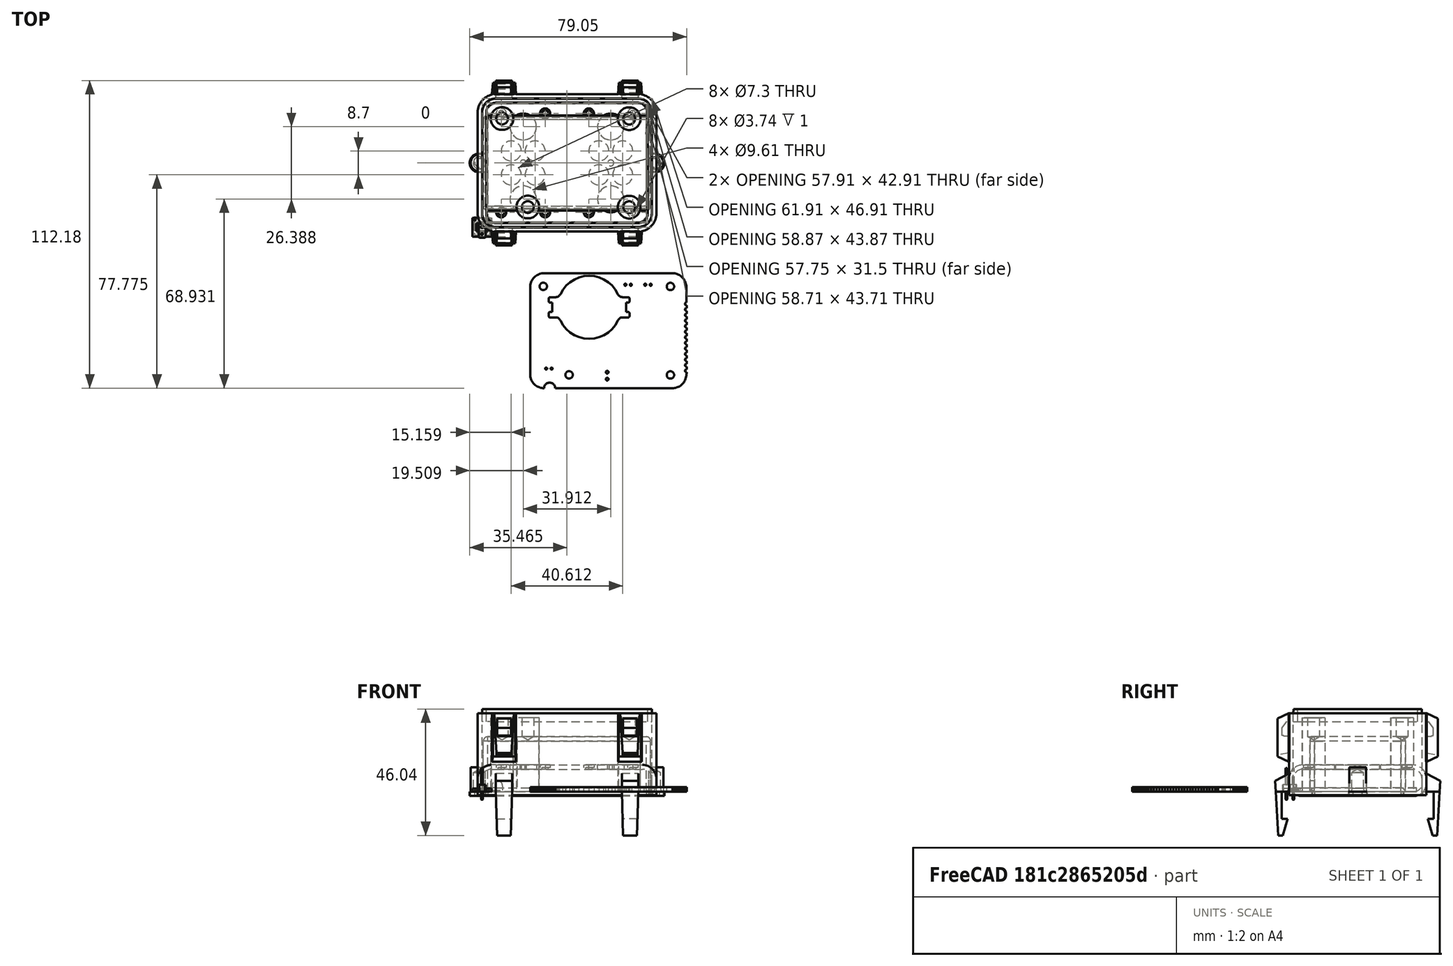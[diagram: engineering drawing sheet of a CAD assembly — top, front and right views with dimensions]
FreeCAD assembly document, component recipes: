
FREECAD ASSEMBLY — COMPONENT RECIPES ("Enclosure")

This assembly document has 16 components, labeled P0..P15 below (a component is one placed body or linked part). 15 of them carry a construction recipe — the FreeCAD feature program that regenerates the part from scratch, quoted from this document or its linked companion documents; the rest are supplied as boundary geometry only. No exploded tour is included for this assembly.
COMPONENT P0 — recipe-attached ("Body002", modeled in this document).
Construction recipe (the document's own serialized feature program — sketch geometry with constraints, then the solid features built on it; lengths are millimeters unless a unit is written):

FEATURE [Sketcher::SketchObject] Sketch003
  FullyConstrained = true
  MapMode = 5
  Support = -> [XY_Plane039]
  expr: Constraints[10] = <<dim>>.encw
  expr: Constraints[9] = <<dim>>.encl
  sketch-geometry (4):
    g0: LineSegment StartX=0 StartY=0 StartZ=0 EndX=61.91 EndY=0 EndZ=0
    g1: LineSegment StartX=61.91 StartY=0 StartZ=0 EndX=61.91 EndY=46.91 EndZ=0
    g2: LineSegment StartX=61.91 StartY=46.91 StartZ=0 EndX=0 EndY=46.91 EndZ=0
    g3: LineSegment StartX=0 StartY=46.91 StartZ=0 EndX=0 EndY=0 EndZ=0
  constraints (11):
    c: Coincident(g0,g1)
    c: Coincident(g1,g2)
    c: Coincident(g2,g3)
    c: Coincident(g3,g0)
    c: Horizontal(g0)
    c: Horizontal(g2)
    c: Vertical(g1)
    c: Vertical(g3)
    c: Coincident(g0,g-1)
    c: Distance(g2) = 61.91
    c: Distance(g1) = 46.91
FEATURE [PartDesign::Pad] Pad002
  Direction = (0,0,1)
  Length = 28.535
  Length2 = 10
  Profile = -> Sketch003
  ReferenceAxis = -> Sketch003 [N_Axis]
  Type = 0
  expr: Length = <<dim>>.ench
FEATURE [PartDesign::Fillet] Fillet001
  Base = -> Pad002 [Edge1,Edge2,Edge3,Edge5,Edge6,Edge8,Edge9,Edge11]
  BaseFeature = -> Pad002
  Radius = 5
  SupportTransform = false
  UseAllEdges = false
  expr: Radius = <<dim>>.encrin
FEATURE [PartDesign::Thickness] Thickness002
  Base = -> Fillet001 [Face2]
  BaseFeature = -> Fillet001
  Intersection = false
  Join = 0
  Mode = 0
  Reversed = true
  SupportTransform = false
  Value = 1.6
  expr: Value = <<dim>>.enctsh
FEATURE [PartDesign::ShapeBinder] ShapeBinder001
  Support = -> [Thickness002]
  TraceSupport = false
FEATURE [PartDesign::SubShapeBinder] Binder
  BindCopyOnChange = 0
  BindMode = 0
  ClaimChildren = false
  Context = -> Part [Body002.Binder.]
  Fuse = false
  MakeFace = true
  OffsetFill = false
  OffsetIntersection = false
  OffsetJoinType = 0
  OffsetOpenResult = false
  PartialLoad = false
  Placement = pos=(0,0,-3) rot=(0,0,1;0rad)
  Relative = true
  Support = -> [ShapeBinder001]
  _Version = 2
  expr: .Placement.Base.z = -<<dim>>.eid
FEATURE [PartDesign::Pocket] Pocket001
  BaseFeature = -> Thickness002
  Direction = (0,0,-1)
  Length = 5
  Length2 = 5
  Profile = -> Binder
  Type = 1
FEATURE [PartDesign::Pad] Pad013
  BaseFeature = -> Pocket001
  Direction = (0,0,1)
  Length = 1.5
  Length2 = 10
  Profile = -> Pocket001 [Face5]
  TaperAngle = -3
  Type = 0
  expr: Length = <<dim>>.elh
  expr: TaperAngle = <<dim>>.elt
FEATURE [PartDesign::Body] Body002
  Group = -> [Sketch003,Pad002,Fillet001,Thickness002,ShapeBinder001,Binder,Pocket001,Pad013]
  Origin = -> Origin041
  Tip = -> Pad013
COMPONENT P1 — recipe-attached ("batteryboxinner", modeled in this document).
Construction recipe (the document's own serialized feature program — sketch geometry with constraints, then the solid features built on it; lengths are millimeters unless a unit is written):

FEATURE [Sketcher::SketchObject] Sketch010
  FullyConstrained = true
  MapMode = 5
  Support = -> [XY_Plane047]
  expr: Constraints[15] = <<dim>>.batl * (1 + <<dim>>.batc)
  expr: Constraints[16] = <<dim>>.batw * (1 + <<dim>>.batc)
  expr: Constraints[26] = <<dim>>.encl / 2
  expr: Constraints[27] = <<dim>>.encw / 2
  sketch-geometry (12):
    g0: LineSegment StartX=2.08 StartY=7.705 StartZ=0 EndX=59.83 EndY=7.705 EndZ=0
    g1: LineSegment StartX=59.83 StartY=7.705 StartZ=0 EndX=59.83 EndY=39.205 EndZ=0
    g2: LineSegment StartX=59.83 StartY=39.205 StartZ=0 EndX=2.08 EndY=39.205 EndZ=0
    g3: LineSegment StartX=2.08 StartY=39.205 StartZ=0 EndX=2.08 EndY=7.705 EndZ=0
    g4: LineSegment StartX=30.955 StartY=23.455 StartZ=0 EndX=2.08 EndY=23.455 EndZ=0
    g5: LineSegment StartX=2.08 StartY=23.455 StartZ=0 EndX=2.08 EndY=7.705 EndZ=0
    g6: LineSegment StartX=2.08 StartY=7.705 StartZ=0 EndX=30.955 EndY=7.705 EndZ=0
    g7: LineSegment StartX=30.955 StartY=7.705 StartZ=0 EndX=30.955 EndY=23.455 EndZ=0
    g8: LineSegment StartX=0 StartY=0 StartZ=0 EndX=30.955 EndY=0 EndZ=0
    g9: LineSegment StartX=30.955 StartY=0 StartZ=0 EndX=30.955 EndY=23.455 EndZ=0
    g10: LineSegment StartX=30.955 StartY=23.455 StartZ=0 EndX=0 EndY=23.455 EndZ=0
    g11: LineSegment StartX=0 StartY=23.455 StartZ=0 EndX=0 EndY=0 EndZ=0
  constraints (31):
    c: Coincident(g0,g1)
    c: Coincident(g1,g2)
    c: Coincident(g2,g3)
    c: Coincident(g3,g0)
    c: Horizontal(g0)
    c: Horizontal(g2)
    c: Vertical(g1)
    c: Vertical(g3)
    c: Coincident(g4,g5)
    c: Coincident(g5,g6)
    c: Coincident(g6,g7)
    c: Coincident(g7,g4)
    c: Horizontal(g4)
    c: Vertical(g7)
    c: Coincident(g5,g0)
    c: Distance(g2) = 57.75
    c: Distance(g1) = 31.5
    c: Coincident(g8,g9)
    c: Coincident(g9,g10)
    c: Coincident(g10,g11)
    c: Coincident(g11,g8)
    c: Horizontal(g8)
    c: Horizontal(g10)
    c: Vertical(g9)
    c: Vertical(g11)
    c: Coincident(g8,g-1)
    c: Distance(g10) = 30.955
    c: Distance(g9) = 23.455
    c: Coincident(g4,g9)
    c: Symmetric(g0,g0,g6)
    c: Symmetric(g0,g2,g4)
FEATURE [PartDesign::Pad] Pad010
  Direction = (0,0,1)
  Length = 18.375
  Length2 = 10
  Profile = -> Sketch010
  ReferenceAxis = -> Sketch010 [N_Axis]
  Type = 0
  expr: Length = <<dim>>.bath * (1 + <<dim>>.batc)
FEATURE [PartDesign::Pad] Pad012
  BaseFeature = -> Pad010
  Direction = (0,0,-1)
  Length = 1.6
  Length2 = 10
  Profile = -> Pad010 [Face5]
  Type = 0
  expr: Length = <<dim>>.enctsh
FEATURE [PartDesign::Body] Body003  label="batteryboxinner"
  Group = -> [Sketch010,Pad010,Pad012]
  Origin = -> Origin048
  Tip = -> Pad012
COMPONENT P2 — recipe-attached ("batteryboxshell", modeled in this document).
Construction recipe (the document's own serialized feature program — sketch geometry with constraints, then the solid features built on it; lengths are millimeters unless a unit is written):

FEATURE [Sketcher::SketchObject] Sketch011
  FullyConstrained = true
  MapMode = 5
  Support = -> [XY_Plane047]
  expr: Constraints[15] = <<dim>>.batl * (1 + <<dim>>.batc)
  expr: Constraints[16] = <<dim>>.batw * (1 + <<dim>>.batc)
  expr: Constraints[26] = <<dim>>.encl / 2
  expr: Constraints[27] = <<dim>>.encw / 2
  sketch-geometry (12):
    g0: LineSegment StartX=2.08 StartY=7.705 StartZ=0 EndX=59.83 EndY=7.705 EndZ=0
    g1: LineSegment StartX=59.83 StartY=7.705 StartZ=0 EndX=59.83 EndY=39.205 EndZ=0
    g2: LineSegment StartX=59.83 StartY=39.205 StartZ=0 EndX=2.08 EndY=39.205 EndZ=0
    g3: LineSegment StartX=2.08 StartY=39.205 StartZ=0 EndX=2.08 EndY=7.705 EndZ=0
    g4: LineSegment StartX=30.955 StartY=23.455 StartZ=0 EndX=2.08 EndY=23.455 EndZ=0
    g5: LineSegment StartX=2.08 StartY=23.455 StartZ=0 EndX=2.08 EndY=7.705 EndZ=0
    g6: LineSegment StartX=2.08 StartY=7.705 StartZ=0 EndX=30.955 EndY=7.705 EndZ=0
    g7: LineSegment StartX=30.955 StartY=7.705 StartZ=0 EndX=30.955 EndY=23.455 EndZ=0
    g8: LineSegment StartX=0 StartY=0 StartZ=0 EndX=30.955 EndY=0 EndZ=0
    g9: LineSegment StartX=30.955 StartY=0 StartZ=0 EndX=30.955 EndY=23.455 EndZ=0
    g10: LineSegment StartX=30.955 StartY=23.455 StartZ=0 EndX=0 EndY=23.455 EndZ=0
    g11: LineSegment StartX=0 StartY=23.455 StartZ=0 EndX=0 EndY=0 EndZ=0
  constraints (31):
    c: Coincident(g0,g1)
    c: Coincident(g1,g2)
    c: Coincident(g2,g3)
    c: Coincident(g3,g0)
    c: Horizontal(g0)
    c: Horizontal(g2)
    c: Vertical(g1)
    c: Vertical(g3)
    c: Coincident(g4,g5)
    c: Coincident(g5,g6)
    c: Coincident(g6,g7)
    c: Coincident(g7,g4)
    c: Horizontal(g4)
    c: Vertical(g7)
    c: Coincident(g5,g0)
    c: Distance(g2) = 57.75
    c: Distance(g1) = 31.5
    c: Coincident(g8,g9)
    c: Coincident(g9,g10)
    c: Coincident(g10,g11)
    c: Coincident(g11,g8)
    c: Horizontal(g8)
    c: Horizontal(g10)
    c: Vertical(g9)
    c: Vertical(g11)
    c: Coincident(g8,g-1)
    c: Distance(g10) = 30.955
    c: Distance(g9) = 23.455
    c: Coincident(g4,g9)
    c: Symmetric(g0,g0,g6)
    c: Symmetric(g0,g2,g4)
FEATURE [PartDesign::Pad] Pad011
  Direction = (0,0,1)
  Length = 18.375
  Length2 = 10
  Profile = -> Sketch011
  ReferenceAxis = -> Sketch011 [N_Axis]
  Type = 0
  expr: Length = <<dim>>.bath * (1 + <<dim>>.batc)
FEATURE [PartDesign::Thickness] Thickness001
  Base = -> Pad011 [Face5]
  BaseFeature = -> Pad011
  Intersection = false
  Join = 0
  Mode = 0
  SupportTransform = false
  Value = 1.6
  expr: Value = <<dim>>.enctsh
FEATURE [Sketcher::SketchObject] Sketch012
  FullyConstrained = false
  MapMode = 5
  Placement = pos=(0,6.105,0) rot=(1,0,0;1.5708rad)
  Support = -> [Thickness001]
  expr: Constraints[10] = <<dim>>.enctsh
  expr: Constraints[11] = <<dim>>.batl * (<<dim>>.batc + 1) / 30
  expr: Constraints[9] = (<<dim>>.encl - <<dim>>.batl * (1 + <<dim>>.batc)) / 2
  sketch-geometry (5):
    g0: ArcOfCircle CenterX=5.55399 CenterY=2.00077 CenterZ=0 NormalX=0 NormalY=0 NormalZ=1 AngleXU=0 Radius=1.925 StartAngle=0 EndAngle=3.14159
    g1: LineSegment StartX=7.47899 StartY=0.400772 StartZ=0 EndX=7.47899 EndY=2.00077 EndZ=0
    g2: LineSegment StartX=3.62899 StartY=2.00077 StartZ=0 EndX=3.62899 EndY=0.400772 EndZ=0
    g3: LineSegment StartX=3.62899 StartY=0.400772 StartZ=0 EndX=7.47899 EndY=0.400772 EndZ=0
    g4: LineSegment StartX=0 StartY=0 StartZ=0 EndX=2.08 EndY=0 EndZ=0
  constraints (12):
    c: Tangent(g1,g0) = -1.5708
    c: Tangent(g0,g2) = -1.5708
    c: Vertical(g1)
    c: Horizontal(g3)
    c: Coincident(g2,g3)
    c: Coincident(g1,g3)
    c: Vertical(g2)
    c: Coincident(g4,g-1)
    c: PointOnObject(g4,g-1)
    c: Distance(g4) = 2.08
    c: Distance(g1,g0) = 1.6
    c: Radius(g0) = 1.925
FEATURE [PartDesign::Pocket] Pocket
  BaseFeature = -> Thickness001
  Direction = (0,1,-2e-16)
  Length = 1.6
  Length2 = 5
  Profile = -> Sketch012
  ReferenceAxis = -> Sketch012 [N_Axis]
  Type = 0
  expr: Length = <<dim>>.enctsh
FEATURE [PartDesign::Body] Body004  label="batteryboxshell"
  Group = -> [Sketch011,Pad011,Thickness001,Sketch012,Pocket]
  Origin = -> Origin049
  Tip = -> Pocket
COMPONENT P3 — recipe-attached ("batterydoorneg", modeled in this document).
Construction recipe (the document's own serialized feature program — sketch geometry with constraints, then the solid features built on it; lengths are millimeters unless a unit is written):

FEATURE [Sketcher::SketchObject] Sketch013
  FullyConstrained = true
  MapMode = 5
  Support = -> [XY_Plane047]
  expr: Constraints[15] = <<dim>>.batl * (1 + <<dim>>.batc) + <<dim>>.enctsh + 2 * <<dim>>.enctol
  expr: Constraints[16] = <<dim>>.batw * (1 + <<dim>>.batc) + <<dim>>.enctsh + 2 * <<dim>>.enctol
  expr: Constraints[26] = <<dim>>.encl / 2
  expr: Constraints[27] = <<dim>>.encw / 2
  expr: Constraints[47] = (<<dim>>.hid + <<dim>>.hit) / 2 + <<dim>>.enctol
  expr: Constraints[48] = <<dim>>.hid / 2
  sketch-geometry (22):
    g0: LineSegment StartX=1.026 StartY=6.651 StartZ=0 EndX=60.884 EndY=6.651 EndZ=0
    g1: LineSegment StartX=60.884 StartY=6.651 StartZ=0 EndX=60.884 EndY=40.259 EndZ=0
    g2: LineSegment StartX=60.884 StartY=40.259 StartZ=0 EndX=1.026 EndY=40.259 EndZ=0
    g3: LineSegment StartX=1.026 StartY=40.259 StartZ=0 EndX=1.026 EndY=6.651 EndZ=0
    g4: LineSegment StartX=30.955 StartY=23.455 StartZ=0 EndX=1.026 EndY=23.455 EndZ=0
    g5: LineSegment StartX=1.026 StartY=23.455 StartZ=0 EndX=1.026 EndY=6.651 EndZ=0
    g6: LineSegment StartX=1.026 StartY=6.651 StartZ=0 EndX=30.955 EndY=6.651 EndZ=0
    g7: LineSegment StartX=30.955 StartY=6.651 StartZ=0 EndX=30.955 EndY=23.455 EndZ=0
    g8: LineSegment StartX=0 StartY=0 StartZ=0 EndX=30.955 EndY=0 EndZ=0
    g9: LineSegment StartX=30.955 StartY=0 StartZ=0 EndX=30.955 EndY=23.455 EndZ=0
    g10: LineSegment StartX=30.955 StartY=23.455 StartZ=0 EndX=0 EndY=23.455 EndZ=0
    g11: LineSegment StartX=0 StartY=23.455 StartZ=0 EndX=0 EndY=0 EndZ=0
    g12: ArcOfCircle CenterX=-1.113 CenterY=23.455 CenterZ=0 NormalX=0 NormalY=0 NormalZ=1 AngleXU=0 Radius=3.393 StartAngle=1.5708 EndAngle=4.71239
    g13: ArcOfCircle CenterX=63.023 CenterY=23.455 CenterZ=0 NormalX=0 NormalY=0 NormalZ=1 AngleXU=0 Radius=3.393 StartAngle=4.71239 EndAngle=7.85398
    g14: LineSegment StartX=60.884 StartY=20.062 StartZ=0 EndX=63.023 EndY=20.062 EndZ=0
    g15: LineSegment StartX=-1.11301 StartY=20.062 StartZ=0 EndX=1.026 EndY=20.062 EndZ=0
    g16: LineSegment StartX=1.026 StartY=26.848 StartZ=0 EndX=-1.113 EndY=26.848 EndZ=0
    g17: LineSegment StartX=63.023 StartY=26.848 StartZ=0 EndX=60.884 EndY=26.848 EndZ=0
    g18: LineSegment StartX=1.026 StartY=26.848 StartZ=0 EndX=1.026 EndY=40.259 EndZ=0
    g19: LineSegment StartX=1.026 StartY=20.062 StartZ=0 EndX=1.026 EndY=6.651 EndZ=0
    g20: LineSegment StartX=60.884 StartY=26.848 StartZ=0 EndX=60.884 EndY=40.259 EndZ=0
    g21: LineSegment StartX=60.884 StartY=20.062 StartZ=0 EndX=60.884 EndY=6.651 EndZ=0
  constraints (57):
    c: Coincident(g0,g1)
    c: Coincident(g1,g2)
    c: Coincident(g2,g3)
    c: Coincident(g3,g0)
    c: Horizontal(g0)
    c: Horizontal(g2)
    c: Vertical(g1)
    c: Vertical(g3)
    c: Coincident(g4,g5)
    c: Coincident(g5,g6)
    c: Coincident(g6,g7)
    c: Coincident(g7,g4)
    c: Horizontal(g4)
    c: Vertical(g7)
    c: Coincident(g5,g0)
    c: Distance(g2) = 59.858
    c: Distance(g1) = 33.608
    c: Coincident(g8,g9)
    c: Coincident(g9,g10)
    c: Coincident(g10,g11)
    c: Coincident(g11,g8)
    c: Horizontal(g8)
    c: Horizontal(g10)
    c: Vertical(g9)
    c: Vertical(g11)
    c: Coincident(g8,g-1)
    c: Distance(g10) = 30.955
    c: Distance(g9) = 23.455
    c: Coincident(g4,g9)
    c: Symmetric(g0,g0,g6)
    c: Symmetric(g0,g2,g4)
    c: Coincident(g12,g15) = -1.5708
    c: Coincident(g14,g13) = -1.5708
    c: Equal(g12,g13)
    c: PointOnObject(g12,g10)
    c: Horizontal(g14)
    c: Horizontal(g15)
    c: PointOnObject(g16,g3)
    c: PointOnObject(g14,g1)
    c: PointOnObject(g17,g1)
    c: Symmetric(g12,g13,g4)
    c: Horizontal(g16)
    c: Horizontal(g17)
    c: Tangent(g16,g12) = -1.5708
    c: Tangent(g13,g17) = -1.5708
    c: Symmetric(g15,g16,g4)
    c: Horizontal(g15,g14)
    c: Radius(g12) = 3.393
    c: Distance(g16) = 2.139
    c: Coincident(g18,g16)
    c: Coincident(g18,g2)
    c: Coincident(g19,g15)
    c: Coincident(g19,g0)
    c: Coincident(g20,g17)
    c: Coincident(g20,g1)
    c: Coincident(g21,g14)
    c: Coincident(g21,g0)
FEATURE [PartDesign::Pad] Pad014
  Direction = (0,0,1)
  Length = 1.6
  Length2 = 10
  Profile = -> Sketch013
  ReferenceAxis = -> Sketch013 [N_Axis]
  Reversed = true
  Type = 0
  expr: Length = <<dim>>.enctsh
FEATURE [PartDesign::Body] Body005  label="batterydoorneg"
  Group = -> [Sketch013,Pad014]
  Origin = -> Origin050
  Tip = -> Pad014
  expr: .Placement.Base.z = 0
COMPONENT P4 — recipe-attached ("batterydoorpos1", modeled in this document).
Construction recipe (the document's own serialized feature program — sketch geometry with constraints, then the solid features built on it; lengths are millimeters unless a unit is written):

FEATURE [Sketcher::SketchObject] Sketch014
  FullyConstrained = true
  MapMode = 5
  Support = -> [XY_Plane047]
  expr: Constraints[15] = <<dim>>.batl * (1 + <<dim>>.batc) + <<dim>>.enctsh + <<dim>>.enctol
  expr: Constraints[16] = <<dim>>.batw * (1 + <<dim>>.batc) + <<dim>>.enctsh
  expr: Constraints[26] = <<dim>>.encl / 2
  expr: Constraints[27] = <<dim>>.encw / 2
  expr: Constraints[38] = (<<dim>>.hid + <<dim>>.hit) / 2
  expr: Constraints[39] = <<dim>>.hid / 2
  sketch-geometry (16):
    g0: LineSegment StartX=1.153 StartY=6.905 StartZ=0 EndX=60.757 EndY=6.905 EndZ=0
    g1: LineSegment StartX=60.757 StartY=6.905 StartZ=0 EndX=60.757 EndY=40.005 EndZ=0
    g2: LineSegment StartX=60.757 StartY=40.005 StartZ=0 EndX=1.153 EndY=40.005 EndZ=0
    g3: LineSegment StartX=1.153 StartY=40.005 StartZ=0 EndX=1.153 EndY=6.905 EndZ=0
    g4: LineSegment StartX=30.955 StartY=23.455 StartZ=0 EndX=1.153 EndY=23.455 EndZ=0
    g5: LineSegment StartX=1.153 StartY=23.455 StartZ=0 EndX=1.153 EndY=6.905 EndZ=0
    g6: LineSegment StartX=1.153 StartY=6.905 StartZ=0 EndX=30.955 EndY=6.905 EndZ=0
    g7: LineSegment StartX=30.955 StartY=6.905 StartZ=0 EndX=30.955 EndY=23.455 EndZ=0
    g8: LineSegment StartX=0 StartY=0 StartZ=0 EndX=30.955 EndY=0 EndZ=0
    g9: LineSegment StartX=30.955 StartY=0 StartZ=0 EndX=30.955 EndY=23.455 EndZ=0
    g10: LineSegment StartX=30.955 StartY=23.455 StartZ=0 EndX=0 EndY=23.455 EndZ=0
    g11: LineSegment StartX=0 StartY=23.455 StartZ=0 EndX=0 EndY=0 EndZ=0
    g12: ArcOfCircle CenterX=-0.986 CenterY=23.455 CenterZ=0 NormalX=0 NormalY=0 NormalZ=1 AngleXU=0 Radius=3.139 StartAngle=1.5708 EndAngle=4.71238
    g13: LineSegment StartX=-0.986021 StartY=20.316 StartZ=0 EndX=1.153 EndY=20.316 EndZ=0
    g14: LineSegment StartX=1.153 StartY=26.594 StartZ=0 EndX=-0.986 EndY=26.594 EndZ=0
    g15: LineSegment StartX=1.153 StartY=26.594 StartZ=0 EndX=1.153 EndY=20.316 EndZ=0
  constraints (42):
    c: Coincident(g0,g1)
    c: Coincident(g1,g2)
    c: Coincident(g2,g3)
    c: Coincident(g3,g0)
    c: Horizontal(g0)
    c: Horizontal(g2)
    c: Vertical(g1)
    c: Vertical(g3)
    c: Coincident(g4,g5)
    c: Coincident(g5,g6)
    c: Coincident(g6,g7)
    c: Coincident(g7,g4)
    c: Horizontal(g4)
    c: Vertical(g7)
    c: Coincident(g5,g0)
    c: Distance(g2) = 59.604
    c: Distance(g1) = 33.1
    c: Coincident(g8,g9)
    c: Coincident(g9,g10)
    c: Coincident(g10,g11)
    c: Coincident(g11,g8)
    c: Horizontal(g8)
    c: Horizontal(g10)
    c: Vertical(g9)
    c: Vertical(g11)
    c: Coincident(g8,g-1)
    c: Distance(g10) = 30.955
    c: Distance(g9) = 23.455
    c: Coincident(g4,g9)
    c: Symmetric(g0,g0,g6)
    c: Symmetric(g0,g2,g4)
    c: Coincident(g12,g13) = -1.5708
    c: PointOnObject(g12,g10)
    c: Horizontal(g13)
    c: PointOnObject(g14,g3)
    c: Horizontal(g14)
    c: Tangent(g14,g12) = -1.5708
    c: Symmetric(g13,g14,g4)
    c: Radius(g12) = 3.139
    c: Distance(g14) = 2.139
    c: Coincident(g15,g14)
    c: Coincident(g15,g13)
FEATURE [PartDesign::Pad] Pad015
  Direction = (0,0,1)
  Length = 8.88
  Length2 = 10
  Profile = -> Sketch014
  ReferenceAxis = -> Sketch014 [N_Axis]
  Type = 0
  expr: Length = (<<dim>>.enctsh + <<dim>>.hil) * <<dim>>.hif
FEATURE [PartDesign::Body] Body006  label="batterydoorpos1"
  Group = -> [Sketch014,Pad015]
  Origin = -> Origin051
  Tip = -> Pad015
  expr: .Placement.Base.z = 0
COMPONENT P5 — recipe-attached ("batterydoorpos2", modeled in this document).
Construction recipe (the document's own serialized feature program — sketch geometry with constraints, then the solid features built on it; lengths are millimeters unless a unit is written):

FEATURE [Sketcher::SketchObject] Sketch016
  FullyConstrained = true
  MapMode = 5
  Support = -> [XY_Plane047]
  expr: Constraints[15] = <<dim>>.batl * (1 + <<dim>>.batc) + <<dim>>.enctsh + <<dim>>.enctol
  expr: Constraints[16] = <<dim>>.batw * (1 + <<dim>>.batc) + <<dim>>.enctsh
  expr: Constraints[26] = <<dim>>.encl / 2
  expr: Constraints[27] = <<dim>>.encw / 2
  expr: Constraints[47] = (<<dim>>.hid + <<dim>>.hit) / 2
  expr: Constraints[48] = <<dim>>.hid / 2
  sketch-geometry (21):
    g0: LineSegment StartX=1.153 StartY=6.905 StartZ=0 EndX=60.757 EndY=6.905 EndZ=0
    g1: LineSegment StartX=60.757 StartY=6.905 StartZ=0 EndX=60.757 EndY=40.005 EndZ=0
    g2: LineSegment StartX=60.757 StartY=40.005 StartZ=0 EndX=1.153 EndY=40.005 EndZ=0
    g3: LineSegment StartX=1.153 StartY=40.005 StartZ=0 EndX=1.153 EndY=6.905 EndZ=0
    g4: LineSegment StartX=30.955 StartY=23.455 StartZ=0 EndX=1.153 EndY=23.455 EndZ=0
    g5: LineSegment StartX=1.153 StartY=23.455 StartZ=0 EndX=1.153 EndY=6.905 EndZ=0
    g6: LineSegment StartX=1.153 StartY=6.905 StartZ=0 EndX=30.955 EndY=6.905 EndZ=0
    g7: LineSegment StartX=30.955 StartY=6.905 StartZ=0 EndX=30.955 EndY=23.455 EndZ=0
    g8: LineSegment StartX=0 StartY=0 StartZ=0 EndX=30.955 EndY=0 EndZ=0
    g9: LineSegment StartX=30.955 StartY=0 StartZ=0 EndX=30.955 EndY=23.455 EndZ=0
    g10: LineSegment StartX=30.955 StartY=23.455 StartZ=0 EndX=0 EndY=23.455 EndZ=0
    g11: LineSegment StartX=0 StartY=23.455 StartZ=0 EndX=0 EndY=0 EndZ=0
    g12: ArcOfCircle CenterX=-0.986 CenterY=23.455 CenterZ=0 NormalX=0 NormalY=0 NormalZ=1 AngleXU=0 Radius=3.139 StartAngle=1.5708 EndAngle=4.71238
    g13: ArcOfCircle CenterX=62.896 CenterY=23.455 CenterZ=0 NormalX=0 NormalY=0 NormalZ=1 AngleXU=0 Radius=3.139 StartAngle=4.71239 EndAngle=7.85398
    g14: LineSegment StartX=60.757 StartY=20.316 StartZ=0 EndX=62.896 EndY=20.316 EndZ=0
    g15: LineSegment StartX=-0.986016 StartY=20.316 StartZ=0 EndX=1.153 EndY=20.316 EndZ=0
    g16: LineSegment StartX=1.153 StartY=26.594 StartZ=0 EndX=-0.986 EndY=26.594 EndZ=0
    g17: LineSegment StartX=62.896 StartY=26.594 StartZ=0 EndX=60.757 EndY=26.594 EndZ=0
    g18: LineSegment StartX=60.757 StartY=26.594 StartZ=0 EndX=60.757 EndY=40.005 EndZ=0
    g19: LineSegment StartX=60.757 StartY=20.316 StartZ=0 EndX=60.757 EndY=6.905 EndZ=0
    g20: LineSegment StartX=60.757 StartY=20.316 StartZ=0 EndX=60.757 EndY=26.594 EndZ=0
  constraints (55):
    c: Coincident(g0,g1)
    c: Coincident(g1,g2)
    c: Coincident(g2,g3)
    c: Coincident(g3,g0)
    c: Horizontal(g0)
    c: Horizontal(g2)
    c: Vertical(g1)
    c: Vertical(g3)
    c: Coincident(g4,g5)
    c: Coincident(g5,g6)
    c: Coincident(g6,g7)
    c: Coincident(g7,g4)
    c: Horizontal(g4)
    c: Vertical(g7)
    c: Coincident(g5,g0)
    c: Distance(g2) = 59.604
    c: Distance(g1) = 33.1
    c: Coincident(g8,g9)
    c: Coincident(g9,g10)
    c: Coincident(g10,g11)
    c: Coincident(g11,g8)
    c: Horizontal(g8)
    c: Horizontal(g10)
    c: Vertical(g9)
    c: Vertical(g11)
    c: Coincident(g8,g-1)
    c: Distance(g10) = 30.955
    c: Distance(g9) = 23.455
    c: Coincident(g4,g9)
    c: Symmetric(g0,g0,g6)
    c: Symmetric(g0,g2,g4)
    c: Coincident(g12,g15) = -1.5708
    c: Coincident(g14,g13) = -1.5708
    c: Equal(g12,g13)
    c: PointOnObject(g12,g10)
    c: Horizontal(g14)
    c: Horizontal(g15)
    c: PointOnObject(g16,g3)
    c: PointOnObject(g14,g1)
    c: PointOnObject(g17,g1)
    c: Symmetric(g12,g13,g4)
    c: Horizontal(g16)
    c: Horizontal(g17)
    c: Tangent(g16,g12) = -1.5708
    c: Tangent(g13,g17) = -1.5708
    c: Symmetric(g15,g16,g4)
    c: Horizontal(g15,g14)
    c: Radius(g12) = 3.139
    c: Distance(g16) = 2.139
    c: Coincident(g18,g17)
    c: Coincident(g18,g1)
    c: Coincident(g19,g14)
    c: Coincident(g19,g0)
    c: Coincident(g20,g14)
    c: Coincident(g20,g17)
FEATURE [PartDesign::Pad] Pad017
  Direction = (0,0,1)
  Length = 8.88
  Length2 = 10
  Profile = -> Sketch016
  ReferenceAxis = -> Sketch016 [N_Axis]
  Type = 0
  expr: Length = (<<dim>>.enctsh + <<dim>>.hil) * <<dim>>.hif
FEATURE [PartDesign::Body] Body008  label="batterydoorpos2"
  Group = -> [Sketch016,Pad017]
  Origin = -> Origin053
  Tip = -> Pad017
  expr: .Placement.Base.z = 0
COMPONENT P6 — recipe-attached ("Body010", modeled in this document).
Construction recipe (the document's own serialized feature program — sketch geometry with constraints, then the solid features built on it; lengths are millimeters unless a unit is written):

FEATURE [Sketcher::SketchObject] Sketch018
  FullyConstrained = true
  MapMode = 5
  Support = -> [XY_Plane054]
  expr: Constraints[10] = <<dim>>.encw
  expr: Constraints[9] = <<dim>>.encl
  sketch-geometry (4):
    g0: LineSegment StartX=0 StartY=0 StartZ=0 EndX=61.91 EndY=0 EndZ=0
    g1: LineSegment StartX=61.91 StartY=0 StartZ=0 EndX=61.91 EndY=46.91 EndZ=0
    g2: LineSegment StartX=61.91 StartY=46.91 StartZ=0 EndX=0 EndY=46.91 EndZ=0
    g3: LineSegment StartX=0 StartY=46.91 StartZ=0 EndX=0 EndY=0 EndZ=0
  constraints (11):
    c: Coincident(g0,g1)
    c: Coincident(g1,g2)
    c: Coincident(g2,g3)
    c: Coincident(g3,g0)
    c: Horizontal(g0)
    c: Horizontal(g2)
    c: Vertical(g1)
    c: Vertical(g3)
    c: Coincident(g0,g-1)
    c: Distance(g2) = 61.91
    c: Distance(g1) = 46.91
FEATURE [PartDesign::Pad] Pad019
  Direction = (0,0,1)
  Length = 1.35
  Length2 = 10
  Profile = -> Sketch018
  ReferenceAxis = -> Sketch018 [N_Axis]
  Type = 0
  expr: Length = <<dim>>.elh - <<dim>>.elc
FEATURE [PartDesign::Fillet] Fillet005
  Base = -> Pad019 [Edge1,Edge2,Edge8,Edge5]
  BaseFeature = -> Pad019
  Radius = 5
  SupportTransform = false
  UseAllEdges = false
  expr: Radius = <<dim>>.encrin
FEATURE [PartDesign::Thickness] Thickness004
  Base = -> Fillet005 [Face2,Face5]
  BaseFeature = -> Fillet005
  Intersection = false
  Join = 0
  Mode = 0
  Reversed = true
  SupportTransform = false
  Value = 2
  expr: Value = <<dim>>.pcbctop
FEATURE [PartDesign::Body] Body010
  Group = -> [Sketch018,Pad019,Fillet005,Thickness004]
  Origin = -> Origin056
  Tip = -> Thickness004
COMPONENT P7 — recipe-attached ("Body011", modeled in this document).
Construction recipe (the document's own serialized feature program — sketch geometry with constraints, then the solid features built on it; lengths are millimeters unless a unit is written):

FEATURE [Sketcher::SketchObject] Sketch019
  FullyConstrained = true
  MapMode = 5
  Support = -> [XY_Plane054]
  expr: Constraints[10] = <<dim>>.encw
  expr: Constraints[9] = <<dim>>.encl
  sketch-geometry (4):
    g0: LineSegment StartX=0 StartY=0 StartZ=0 EndX=61.91 EndY=0 EndZ=0
    g1: LineSegment StartX=61.91 StartY=0 StartZ=0 EndX=61.91 EndY=46.91 EndZ=0
    g2: LineSegment StartX=61.91 StartY=46.91 StartZ=0 EndX=0 EndY=46.91 EndZ=0
    g3: LineSegment StartX=0 StartY=46.91 StartZ=0 EndX=0 EndY=0 EndZ=0
  constraints (11):
    c: Coincident(g0,g1)
    c: Coincident(g1,g2)
    c: Coincident(g2,g3)
    c: Coincident(g3,g0)
    c: Horizontal(g0)
    c: Horizontal(g2)
    c: Vertical(g1)
    c: Vertical(g3)
    c: Coincident(g0,g-1)
    c: Distance(g2) = 61.91
    c: Distance(g1) = 46.91
FEATURE [PartDesign::Pad] Pad021
  Direction = (0,0,1)
  Length = 8.1
  Length2 = 10
  Profile = -> Sketch019
  ReferenceAxis = -> Sketch019 [N_Axis]
  Type = 0
  expr: Length = <<dim>>.pcbctop + <<dim>>.spd
FEATURE [PartDesign::Fillet] Fillet006
  Base = -> Pad021 [Edge1,Edge2,Edge8,Edge5]
  BaseFeature = -> Pad021
  Radius = 5
  SupportTransform = false
  UseAllEdges = false
  expr: Radius = <<dim>>.encrin
FEATURE [PartDesign::Thickness] Thickness005
  Base = -> Fillet006 [Face2,Face5]
  BaseFeature = -> Fillet006
  Intersection = false
  Join = 0
  Mode = 0
  SupportTransform = false
  Value = 0.15
  expr: Value = <<dim>>.elc
FEATURE [PartDesign::Pad] Pad022
  BaseFeature = -> Thickness005
  Direction = (0,0,-1)
  Length = 1.35
  Length2 = 10
  Profile = -> Thickness005 [Face9]
  TaperAngle = 3
  Type = 0
  expr: Length = <<dim>>.elh - <<dim>>.elc
  expr: TaperAngle = -<<dim>>.elt
FEATURE [PartDesign::Pocket] Pocket002
  BaseFeature = -> Pad022
  Direction = (0,0,-1)
  Length = 8.1
  Length2 = 5
  Profile = -> Pad022 [Face5]
  Type = 0
  expr: Length = <<dim>>.pcbctop + <<dim>>.spd
FEATURE [PartDesign::Body] Body011
  Group = -> [Sketch019,Pad021,Fillet006,Thickness005,Pad022,Pocket002]
  Origin = -> Origin057
  Tip = -> Pocket002
COMPONENT P8 — geometry summary ("Elephant0.9.2 1"; no construction recipe available for this part):
  bounding box: 57.0 x 41.9 x 11.5 mm
  tessellated surface: 8,900 triangles
  volume: 3118 mm^3 (11% of its bounding box)
COMPONENT P9 — recipe-attached ("enclosure", modeled in this document).
Construction recipe (the document's own serialized feature program — sketch geometry with constraints, then the solid features built on it; lengths are millimeters unless a unit is written):

FEATURE [Sketcher::SketchObject] Sketch
  FullyConstrained = true
  MapMode = 5
  Support = -> [XY_Plane039]
  expr: Constraints[10] = <<dim>>.encw
  expr: Constraints[9] = <<dim>>.encl
  sketch-geometry (4):
    g0: LineSegment StartX=0 StartY=0 StartZ=0 EndX=61.91 EndY=0 EndZ=0
    g1: LineSegment StartX=61.91 StartY=0 StartZ=0 EndX=61.91 EndY=46.91 EndZ=0
    g2: LineSegment StartX=61.91 StartY=46.91 StartZ=0 EndX=0 EndY=46.91 EndZ=0
    g3: LineSegment StartX=0 StartY=46.91 StartZ=0 EndX=0 EndY=0 EndZ=0
  constraints (11):
    c: Coincident(g0,g1)
    c: Coincident(g1,g2)
    c: Coincident(g2,g3)
    c: Coincident(g3,g0)
    c: Horizontal(g0)
    c: Horizontal(g2)
    c: Vertical(g1)
    c: Vertical(g3)
    c: Coincident(g0,g-1)
    c: Distance(g2) = 61.91
    c: Distance(g1) = 46.91
FEATURE [PartDesign::Pad] Pad001
  Direction = (0,0,1)
  Length = 28.535
  Length2 = 10
  Profile = -> Sketch
  ReferenceAxis = -> Sketch [N_Axis]
  Type = 0
  expr: Length = <<dim>>.ench
FEATURE [PartDesign::Fillet] Fillet
  Base = -> Pad001 [Edge1,Edge2,Edge5,Edge8]
  BaseFeature = -> Pad001
  Radius = 5
  SupportTransform = false
  UseAllEdges = false
  expr: Radius = <<dim>>.encrin
FEATURE [PartDesign::Plane] DatumPlane002
  AttachmentOffset = pos=(0,0,5.5) rot=(0,0,1;0rad)
  Length = 90.7894
  MapMode = 5
  Placement = pos=(5.5,-1.2e-15,1.2e-15) rot=(0.57735,0.57735,0.57735;2.0944rad)
  ResizeMode = 0
  Support = -> [YZ_Plane039]
  Width = 68.1144
  expr: .AttachmentOffset.Base.z = <<dim>>.encrin + (<<hook>>.shouldw - <<hook>>.hookw) / 2
FEATURE [Sketcher::SketchObject] Sketch022
  FullyConstrained = true
  MapMode = 5
  Placement = pos=(5.5,-1.2e-15,1.2e-15) rot=(0.57735,0.57735,0.57735;2.0944rad)
  Support = -> [DatumPlane002]
  expr: Constraints[15] = <<hook>>.hookl / 2
  expr: Constraints[16] = <<hook>>.apd - <<hook>>.hookc
  expr: Constraints[17] = <<hook>>.shaftc * 2
  expr: Constraints[23] = <<hook>>.shaftc
  expr: Constraints[2] = <<dim>>.ench + <<dim>>.elh + <<hook>>.hookc - <<hook>>.shaftl
  expr: Constraints[3] = <<dim>>.enctsh
  sketch-geometry (8):
    g0: LineSegment StartX=-1.6 StartY=0 StartZ=0 EndX=-1.6 EndY=20.135 EndZ=0
    g1: LineSegment StartX=-1.6 StartY=20.135 StartZ=0 EndX=-3.5 EndY=20.135 EndZ=0
    g2: LineSegment StartX=-3.5 StartY=20.135 StartZ=0 EndX=-3.5 EndY=20.435 EndZ=0
    g3: LineSegment StartX=-3.5 StartY=20.435 StartZ=0 EndX=-4.1 EndY=20.435 EndZ=0
    g4: LineSegment StartX=-4.1 StartY=20.435 StartZ=0 EndX=-4.1 EndY=23.135 EndZ=0
    g5: LineSegment StartX=-4.1 StartY=23.135 StartZ=0 EndX=-1.6 EndY=26.635 EndZ=0
    g6: LineSegment StartX=-1.6 StartY=26.635 StartZ=0 EndX=-1.6 EndY=20.435 EndZ=0
    g7: LineSegment StartX=-1.6 StartY=20.435 StartZ=0 EndX=-1.6 EndY=20.135 EndZ=0
  constraints (24):
    c: PointOnObject(g0,g-1)
    c: Vertical(g0)
    c: Distance(g0) = 20.135
    c: Distance(g0,g-1) = 1.6
    c: Coincident(g1,g0)
    c: Horizontal(g1)
    c: Coincident(g2,g1)
    c: Vertical(g2)
    c: Coincident(g3,g2)
    c: Horizontal(g3)
    c: Coincident(g4,g3)
    c: Vertical(g4)
    c: Coincident(g5,g4)
    c: Coincident(g6,g5)
    c: Coincident(g7,g0)
    c: DistanceY(g1,g4) = 3
    c: DistanceX(g3,g0) = 2.5
    c: Distance(g3) = 0.6
    c: Coincident(g6,g7)
    c: Vertical(g6)
    c: Vertical(g7)
    c: Distance(g6,g7) = 6.5
    c: Horizontal(g2,g6)
    c: Distance(g7) = 0.3
FEATURE [PartDesign::Plane] DatumPlane003
  AttachmentOffset = pos=(0,0,30.955) rot=(0,0,1;0rad)
  Length = 90.7894
  MapMode = 5
  Placement = pos=(30.955,-6.9e-15,6.9e-15) rot=(0.57735,0.57735,0.57735;2.0944rad)
  ResizeMode = 0
  Support = -> [YZ_Plane039]
  Width = 68.1144
  expr: .AttachmentOffset.Base.z = <<dim>>.encl / 2
FEATURE [PartDesign::Plane] DatumPlane004
  AttachmentOffset = pos=(0,0,-23.455) rot=(0,0,1;0rad)
  Length = 105.191
  MapMode = 5
  Placement = pos=(0,23.455,5.2e-15) rot=(1,0,0;1.5708rad)
  ResizeMode = 0
  Support = -> [XZ_Plane039]
  Width = 69.1914
  expr: .AttachmentOffset.Base.z = -<<dim>>.encw / 2
FEATURE [PartDesign::Mirrored] Mirrored
  MirrorPlane = -> DatumPlane003
FEATURE [PartDesign::Mirrored] Mirrored001
  MirrorPlane = -> DatumPlane004
FEATURE [PartDesign::Fillet] Fillet007
  Base = -> Fillet [Face2]
  BaseFeature = -> Fillet
  Radius = 3
  SupportTransform = false
  UseAllEdges = false
FEATURE [PartDesign::Thickness] Thickness
  Base = -> Fillet007 [Face4]
  BaseFeature = -> Fillet007
  Intersection = false
  Join = 0
  Mode = 0
  SupportTransform = false
  Value = 1.6
  expr: Value = <<dim>>.enctsh
FEATURE [PartDesign::Boolean] Boolean
  BaseFeature = -> Thickness
  Group = -> [standoffs,standoffs004,standoffs005,standoffs006]
  Type = 0
FEATURE [PartDesign::Boolean] Boolean001
  BaseFeature = -> Boolean
  Group = -> [Body003]
  Type = 1
FEATURE [PartDesign::Boolean] Boolean002
  BaseFeature = -> Boolean001
  Group = -> [Body004]
  Type = 0
FEATURE [PartDesign::Boolean] Boolean003
  BaseFeature = -> Boolean002
  Group = -> [Body005]
  Type = 1
FEATURE [PartDesign::Boolean] Boolean004
  BaseFeature = -> Boolean003
  Group = -> [Body006,Body008]
  Type = 0
FEATURE [PartDesign::Fillet] Fillet002
  Base = -> Boolean004 [Edge38,Edge200]
  BaseFeature = -> Boolean004
  Radius = 0.3
  SupportTransform = false
  UseAllEdges = false
FEATURE [PartDesign::ShapeBinder] ShapeBinder003
  Support = -> [Fillet002]
  TraceSupport = false
FEATURE [PartDesign::Hole] Hole
  BaseFeature = -> Fillet002
  CustomThreadClearance = 0
  Depth = 6.96
  DepthType = 0
  Diameter = 4.278
  DrillForDepth = false
  DrillPoint = 1
  DrillPointAngle = 118
  HoleCutCountersinkAngle = 40
  HoleCutCustomValues = false
  HoleCutDepth = 0
  HoleCutDiameter = 4.4919
  HoleCutType = 0
  ModelThread = false
  Profile = -> ShapeBinder003
  Tapered = false
  TaperedAngle = 90
  ThreadClass = 0
  ThreadDepth = 6.96
  ThreadDepthType = 0
  ThreadDirection = 0
  ThreadFit = 0
  ThreadSize = 0
  ThreadType = 0
  Threaded = false
  UseCustomThreadClearance = false
  expr: Depth = <<dim>>.hil * <<dim>>.hif
  expr: Diameter = <<dim>>.hid
  expr: HoleCutDiameter = <<dim>>.hid * 1.05
FEATURE [PartDesign::ShapeBinder] ShapeBinder002
  Support = -> [Hole]
  TraceSupport = false
FEATURE [PartDesign::Hole] Hole001
  BaseFeature = -> Hole
  CustomThreadClearance = 0
  Depth = 6.96
  DepthType = 0
  Diameter = 4.278
  DrillForDepth = false
  DrillPoint = 1
  DrillPointAngle = 118
  HoleCutCountersinkAngle = 10
  HoleCutCustomValues = false
  HoleCutDepth = 0
  HoleCutDiameter = 4.4919
  HoleCutType = 2
  ModelThread = false
  Profile = -> ShapeBinder002
  Tapered = false
  TaperedAngle = 90
  ThreadClass = 0
  ThreadDepth = 6.96
  ThreadDepthType = 0
  ThreadDirection = 0
  ThreadFit = 0
  ThreadSize = 0
  ThreadType = 0
  Threaded = false
  UseCustomThreadClearance = false
  expr: Depth = <<dim>>.hil * <<dim>>.hif
  expr: Diameter = <<dim>>.hid
  expr: HoleCutDiameter = <<dim>>.hid * 1.05
FEATURE [PartDesign::Boolean] Boolean007
  BaseFeature = -> Hole001
  Group = -> [Body002]
  Type = 0
FEATURE [PartDesign::Pad] Pad024
  BaseFeature = -> Boolean007
  Direction = (1,-1e-16,1e-16)
  Length = 5.1
  Length2 = 10
  Profile = -> Sketch022
  ReferenceAxis = -> Sketch022 [N_Axis]
  Type = 0
  expr: Length = <<hook>>.hookw + <<hook>>.hookc
FEATURE [PartDesign::MultiTransform] MultiTransform
  BaseFeature = -> Pad024
  Originals = -> [Pad024]
  Transformations = -> [Mirrored,Mirrored001]
FEATURE [PartDesign::Plane] DatumPlane006
  AttachmentOffset = pos=(0,0,0.8) rot=(0,0,1;0rad)
  Length = 105.191
  MapMode = 5
  Placement = pos=(0,-0.8,-2e-16) rot=(1,0,0;1.5708rad)
  ResizeMode = 0
  Support = -> [XZ_Plane039]
  Width = 69.1914
  expr: .AttachmentOffset.Base.z = <<dim>>.enctsh / 2
FEATURE [Sketcher::SketchObject] Sketch028
  FullyConstrained = true
  MapMode = 5
  Placement = pos=(0,-0.8,-2e-16) rot=(1,0,0;1.5708rad)
  Support = -> [DatumPlane006]
  expr: Constraints[10] = <<dim>>.encrin - <<dim>>.enctol + (<<hook>>.shouldw - <<hook>>.hookw) / 2
  expr: Constraints[11] = <<hook>>.shouldl + <<hook>>.shaftl + <<hook>>.hookl + <<hook>>.hookc - (<<dim>>.pcbctop + <<dim>>.spd)
  expr: Constraints[12] = <<dim>>.enctsh
  expr: Constraints[15] = <<dim>>.enctsh / 2
  expr: Constraints[33] = <<hook>>.shouldw - (<<hook>>.shouldw - <<hook>>.hookw) / 2
  expr: Constraints[34] = <<dim>>.enctsh * 2
  expr: Constraints[9] = <<dim>>.ench
  sketch-geometry (12):
    g0: LineSegment StartX=3.646 StartY=28.535 StartZ=0 EndX=4.446 EndY=28.535 EndZ=0
    g1: LineSegment StartX=4.446 StartY=28.535 StartZ=0 EndX=5.246 EndY=14.035 EndZ=0
    g2: LineSegment StartX=5.246 StartY=14.035 StartZ=0 EndX=3.646 EndY=14.035 EndZ=0
    g3: LineSegment StartX=3.646 StartY=14.035 StartZ=0 EndX=3.646 EndY=28.535 EndZ=0
    g4: LineSegment StartX=5.246 StartY=28.535 StartZ=0 EndX=5.246 EndY=0 EndZ=0
    g5: LineSegment StartX=3.646 StartY=14.035 StartZ=0 EndX=3.646 EndY=10.835 EndZ=0
    g6: LineSegment StartX=3.646 StartY=10.835 StartZ=0 EndX=12.346 EndY=10.835 EndZ=0
    g7: LineSegment StartX=12.346 StartY=10.835 StartZ=0 EndX=12.346 EndY=28.535 EndZ=0
    g8: LineSegment StartX=12.346 StartY=28.535 StartZ=0 EndX=11.546 EndY=28.535 EndZ=0
    g9: LineSegment StartX=11.546 StartY=28.535 StartZ=0 EndX=10.746 EndY=14.035 EndZ=0
    g10: LineSegment StartX=10.746 StartY=14.035 StartZ=0 EndX=5.246 EndY=14.035 EndZ=0
    g11: LineSegment StartX=10.746 StartY=14.035 StartZ=0 EndX=12.346 EndY=14.035 EndZ=0
  constraints (36):
    c: Coincident(g0,g1)
    c: Coincident(g1,g2)
    c: Coincident(g2,g3)
    c: Coincident(g3,g0)
    c: Horizontal(g0)
    c: Horizontal(g2)
    c: Vertical(g3)
    c: PointOnObject(g4,g-1)
    c: Vertical(g4)
    c: Distance(g4) = 28.535
    c: Distance(g-1,g4) = 5.246
    c: Distance(g3) = 14.5
    c: Distance(g2) = 1.6
    c: PointOnObject(g1,g4)
    c: Horizontal(g0,g4)
    c: Distance(g0) = 0.8
    c: Coincident(g5,g2)
    c: Vertical(g5)
    c: Horizontal(g6)
    c: Coincident(g7,g6)
    c: Vertical(g7)
    c: Coincident(g8,g7)
    c: Horizontal(g8)
    c: Coincident(g10,g9)
    c: Coincident(g10,g1)
    c: Horizontal(g10)
    c: Horizontal(g0,g9)
    c: Coincident(g8,g9)
    c: Coincident(g11,g9)
    c: PointOnObject(g11,g7)
    c: Horizontal(g11)
    c: Equal(g11,g2)
    c: Equal(g0,g8)
    c: Distance(g10) = 5.5
    c: Distance(g5) = 3.2
    c: Coincident(g6,g5)
FEATURE [PartDesign::Pad] Pad026
  BaseFeature = -> MultiTransform
  Direction = (0,-1,-2e-16)
  Length = 5
  Length2 = 10
  Profile = -> Sketch028
  ReferenceAxis = -> Sketch028 [N_Axis]
  Type = 0
  expr: Length = <<dim>>.enctsh / 2 + <<hook>>.apd + <<hook>>.hmind
FEATURE [PartDesign::Chamfer] Chamfer
  Angle = 10
  Base = -> Pad026 [Edge545]
  BaseFeature = -> Pad026
  ChamferType = 2
  FlipDirection = false
  Size = 4.1
  Size2 = 1
  SupportTransform = false
  UseAllEdges = false
  expr: Size = <<hook>>.smaxd * 0.98 - <<dim>>.enctsh / 2
FEATURE [PartDesign::Chamfer] Chamfer001
  Angle = 25
  Base = -> Chamfer [Edge26,Edge27,Edge24]
  BaseFeature = -> Chamfer
  ChamferType = 2
  FlipDirection = true
  Size = 4.1
  Size2 = 1
  SupportTransform = false
  UseAllEdges = false
  expr: Size = <<hook>>.smaxd * 0.98 - <<dim>>.enctsh / 2
FEATURE [PartDesign::Chamfer] Chamfer002
  Angle = 4
  Base = -> Chamfer001 [Edge16,Edge12]
  BaseFeature = -> Chamfer001
  ChamferType = 2
  FlipDirection = true
  Size = 4.1
  Size2 = 1
  SupportTransform = false
  UseAllEdges = false
  expr: Size = <<hook>>.smaxd * 0.98 - <<dim>>.enctsh / 2
FEATURE [PartDesign::Mirrored] Mirrored004
  MirrorPlane = -> DatumPlane004
FEATURE [PartDesign::Mirrored] Mirrored005
  MirrorPlane = -> DatumPlane003
FEATURE [PartDesign::MultiTransform] MultiTransform002
  BaseFeature = -> Chamfer002
  Originals = -> [Pad026,Chamfer,Chamfer001,Chamfer002]
  Transformations = -> [Mirrored004,Mirrored005]
FEATURE [PartDesign::Body] Body001
  Group = -> [Sketch,Pad001,Fillet,Fillet007,Thickness,Boolean,Boolean001,Boolean002,Boolean003,Boolean004,Fillet002,ShapeBinder002,ShapeBinder003,Hole,Hole001,Boolean007,DatumPlane002,Sketch022,Pad024,DatumPlane003,DatumPlane004,MultiTransform,Mirrored,Mirrored001,DatumPlane006,Sketch028,Pad026,Chamfer,Chamfer001,Chamfer002,MultiTransform002,Mirrored004,Mirrored005]
  Origin = -> Origin039
  Tip = -> MultiTransform002
COMPONENT P10 — recipe-attached ("lid", modeled in this document).
Construction recipe (the document's own serialized feature program — sketch geometry with constraints, then the solid features built on it; lengths are millimeters unless a unit is written):

FEATURE [Sketcher::SketchObject] Sketch017
  FullyConstrained = true
  MapMode = 5
  Support = -> [XY_Plane054]
  expr: Constraints[10] = <<dim>>.encw
  expr: Constraints[9] = <<dim>>.encl
  sketch-geometry (4):
    g0: LineSegment StartX=0 StartY=0 StartZ=0 EndX=61.91 EndY=0 EndZ=0
    g1: LineSegment StartX=61.91 StartY=0 StartZ=0 EndX=61.91 EndY=46.91 EndZ=0
    g2: LineSegment StartX=61.91 StartY=46.91 StartZ=0 EndX=0 EndY=46.91 EndZ=0
    g3: LineSegment StartX=0 StartY=46.91 StartZ=0 EndX=0 EndY=0 EndZ=0
  constraints (11):
    c: Coincident(g0,g1)
    c: Coincident(g1,g2)
    c: Coincident(g2,g3)
    c: Coincident(g3,g0)
    c: Horizontal(g0)
    c: Horizontal(g2)
    c: Vertical(g1)
    c: Vertical(g3)
    c: Coincident(g0,g-1)
    c: Distance(g2) = 61.91
    c: Distance(g1) = 46.91
FEATURE [PartDesign::Pad] Pad018
  Direction = (0,0,1)
  Length = 8.1
  Length2 = 10
  Profile = -> Sketch017
  ReferenceAxis = -> Sketch017 [N_Axis]
  Type = 0
  expr: Length = <<dim>>.pcbctop + <<dim>>.spd
FEATURE [PartDesign::Fillet] Fillet003
  Base = -> Pad018 [Edge1,Edge2,Edge8,Edge5]
  BaseFeature = -> Pad018
  Radius = 5
  SupportTransform = false
  UseAllEdges = false
  expr: Radius = <<dim>>.encrin
FEATURE [PartDesign::Fillet] Fillet004
  Base = -> Fillet003 [Face5]
  BaseFeature = -> Fillet003
  Radius = 3.4
  SupportTransform = false
  UseAllEdges = false
  expr: Radius = <<dim>>.encrin - <<dim>>.enctsh
FEATURE [PartDesign::Thickness] Thickness003
  Base = -> Fillet004 [Face4]
  BaseFeature = -> Fillet004
  Intersection = false
  Join = 0
  Mode = 0
  SupportTransform = false
  Value = 1.6
  expr: Value = <<dim>>.enctsh
FEATURE [PartDesign::Pad] Pad020
  BaseFeature = -> Thickness003
  Direction = (0,0,-1)
  Length = 1.35
  Length2 = 10
  Profile = -> Thickness003 [Face18]
  Type = 0
  expr: Length = <<dim>>.elh - <<dim>>.elc
  expr: TaperAngle = <<dim>>.elt - <<dim>>.elt
FEATURE [PartDesign::Boolean] Boolean005
  BaseFeature = -> Pad020
  Group = -> [Body010]
  Type = 0
FEATURE [PartDesign::Boolean] Boolean006
  BaseFeature = -> Boolean005
  Group = -> [Body011]
  Type = 1
FEATURE [PartDesign::Plane] DatumPlane001
  AttachmentOffset = pos=(0,0,9.7) rot=(0,0,1;0rad)
  Length = 60
  MapMode = 5
  Placement = pos=(0,0,9.7) rot=(0,0,1;0rad)
  ResizeMode = 0
  Support = -> [XY_Plane054]
  Width = 60
  expr: .AttachmentOffset.Base.z = <<dim>>.pcbctop + <<dim>>.spd + <<dim>>.enctsh
FEATURE [Sketcher::SketchObject] Sketch020
  FullyConstrained = true
  MapMode = 5
  Placement = pos=(0,0,9.7) rot=(0,0,1;0rad)
  Support = -> [DatumPlane001]
  expr: Constraints[10] = <<dim>>.encw - 2 * (<<dim>>.encrin - <<dim>>.enctsh)
  expr: Constraints[11] = <<dim>>.encl - 2 * (<<dim>>.encrin - <<dim>>.enctsh)
  expr: Constraints[25] = <<dim>>.spw
  expr: Constraints[26] = <<dim>>.spl
  expr: Constraints[27] = <<dim>>.enctsh
  expr: Constraints[40] = <<dim>>.sshl
  expr: Constraints[41] = <<dim>>.sshw
  expr: Constraints[8] = <<dim>>.encrin - <<dim>>.enctsh
  expr: Constraints[9] = <<dim>>.encrin - <<dim>>.enctsh
  sketch-geometry (55):
    g0: LineSegment StartX=3.4 StartY=3.4 StartZ=0 EndX=58.51 EndY=3.4 EndZ=0
    g1: LineSegment StartX=58.51 StartY=3.4 StartZ=0 EndX=58.51 EndY=43.51 EndZ=0
    g2: LineSegment StartX=58.51 StartY=43.51 StartZ=0 EndX=3.4 EndY=43.51 EndZ=0
    g3: LineSegment StartX=3.4 StartY=43.51 StartZ=0 EndX=3.4 EndY=3.4 EndZ=0
    g4: LineSegment StartX=3.4 StartY=23.455 StartZ=0 EndX=58.51 EndY=23.455 EndZ=0
    g5: LineSegment StartX=4.99905 StartY=3.455 StartZ=0 EndX=24.9991 EndY=3.455 EndZ=0
    g6: LineSegment StartX=24.9991 StartY=3.455 StartZ=0 EndX=24.9991 EndY=43.455 EndZ=0
    g7: LineSegment StartX=24.9991 StartY=43.455 StartZ=0 EndX=4.99905 EndY=43.455 EndZ=0
    g8: LineSegment StartX=4.99905 StartY=43.455 StartZ=0 EndX=4.99905 EndY=3.455 EndZ=0
    g9: GeomPoint X=24.9991 Y=23.455 Z=0
    g10: LineSegment StartX=6.99905 StartY=5.455 StartZ=0 EndX=22.9991 EndY=5.455 EndZ=0
    g11: LineSegment StartX=22.9991 StartY=5.455 StartZ=0 EndX=22.9991 EndY=41.455 EndZ=0
    g12: LineSegment StartX=22.9991 StartY=41.455 StartZ=0 EndX=6.99905 EndY=41.455 EndZ=0
    g13: LineSegment StartX=6.99905 StartY=41.455 StartZ=0 EndX=6.99905 EndY=5.455 EndZ=0
    g14: GeomPoint X=22.9991 Y=23.455 Z=0
    g15: GeomPoint X=14.9991 Y=23.455 Z=0
    g16: GeomPoint X=14.9991 Y=23.455 Z=0
    g17: ArcOfCircle CenterX=14.9991 CenterY=33.455 CenterZ=0 NormalX=0 NormalY=0 NormalZ=1 AngleXU=0 Radius=8 StartAngle=4e-16 EndAngle=3.14159
    g18: ArcOfCircle CenterX=14.9991 CenterY=13.455 CenterZ=0 NormalX=0 NormalY=0 NormalZ=1 AngleXU=0 Radius=8 StartAngle=3.14159 EndAngle=6.28319
    g19: LineSegment StartX=6.99905 StartY=33.455 StartZ=0 EndX=6.99905 EndY=13.455 EndZ=0
    g20: LineSegment StartX=22.9991 StartY=13.455 StartZ=0 EndX=22.9991 EndY=33.455 EndZ=0
    g21: Circle CenterX=6.99905 CenterY=41.455 CenterZ=0 NormalX=0 NormalY=0 NormalZ=1 AngleXU=0 Radius=1.1
    g22: Circle CenterX=22.9991 CenterY=41.455 CenterZ=0 NormalX=0 NormalY=0 NormalZ=1 AngleXU=0 Radius=1.1
    g23: Circle CenterX=6.99905 CenterY=5.455 CenterZ=0 NormalX=0 NormalY=0 NormalZ=1 AngleXU=0 Radius=1.1
    g24: Circle CenterX=22.9991 CenterY=5.455 CenterZ=0 NormalX=0 NormalY=0 NormalZ=1 AngleXU=0 Radius=1.1
    g25: LineSegment StartX=30.955 StartY=3.4 StartZ=0 EndX=30.955 EndY=43.51 EndZ=0
    g26: Circle CenterX=19.3491 CenterY=27.805 CenterZ=0 NormalX=0 NormalY=0 NormalZ=1 AngleXU=0 Radius=3.65
    g27: Circle CenterX=19.3491 CenterY=19.105 CenterZ=0 NormalX=0 NormalY=0 NormalZ=1 AngleXU=0 Radius=3.65
    g28: Circle CenterX=10.6491 CenterY=19.105 CenterZ=0 NormalX=0 NormalY=0 NormalZ=1 AngleXU=0 Radius=3.65
    g29: Circle CenterX=10.6491 CenterY=27.805 CenterZ=0 NormalX=0 NormalY=0 NormalZ=1 AngleXU=0 Radius=3.65
    g30: Circle CenterX=14.9991 CenterY=36.6491 CenterZ=0 NormalX=0 NormalY=0 NormalZ=1 AngleXU=0 Radius=4.80595
    g31: Circle CenterX=14.9991 CenterY=10.2609 CenterZ=0 NormalX=0 NormalY=0 NormalZ=1 AngleXU=0 Radius=4.80595
    g32: LineSegment StartX=12.26 StartY=15.8297 StartZ=0 EndX=12.8779 EndY=14.5735 EndZ=0
    g33: LineSegment StartX=10.6491 StartY=22.755 StartZ=0 EndX=10.6491 EndY=24.155 EndZ=0
    g34: LineSegment StartX=14.2991 StartY=19.105 StartZ=0 EndX=15.6991 EndY=19.105 EndZ=0
    g35: Circle CenterX=14.9991 CenterY=23.455 CenterZ=0 NormalX=0 NormalY=0 NormalZ=1 AngleXU=0 Radius=1.10183
    g36: LineSegment StartX=14.2199 StartY=24.2341 StartZ=0 EndX=13.23 EndY=25.2241 EndZ=0
    g37: Circle CenterX=46.9109 CenterY=36.6491 CenterZ=0 NormalX=0 NormalY=0 NormalZ=1 AngleXU=0 Radius=4.80595
    g38: Circle CenterX=46.9109 CenterY=10.2609 CenterZ=0 NormalX=0 NormalY=0 NormalZ=1 AngleXU=0 Radius=4.80595
    g39: GeomPoint X=30.955 Y=36.6491 Z=0
    g40: GeomPoint X=30.955 Y=27.805 Z=0
    g41: GeomPoint X=30.955 Y=19.105 Z=0
    g42: GeomPoint X=30.955 Y=10.2609 Z=0
    g43: GeomPoint X=30.955 Y=5.455 Z=0
    g44: GeomPoint X=30.955 Y=41.455 Z=0
    g45: Circle CenterX=42.5609 CenterY=27.805 CenterZ=0 NormalX=0 NormalY=0 NormalZ=1 AngleXU=0 Radius=3.65
    g46: Circle CenterX=51.2609 CenterY=27.805 CenterZ=0 NormalX=0 NormalY=0 NormalZ=1 AngleXU=0 Radius=3.65
    g47: Circle CenterX=42.5609 CenterY=19.105 CenterZ=0 NormalX=0 NormalY=0 NormalZ=1 AngleXU=0 Radius=3.65
    g48: Circle CenterX=51.2609 CenterY=19.105 CenterZ=0 NormalX=0 NormalY=0 NormalZ=1 AngleXU=0 Radius=3.65
    g49: Circle CenterX=38.9109 CenterY=41.455 CenterZ=0 NormalX=0 NormalY=0 NormalZ=1 AngleXU=0 Radius=1.1
    g50: Circle CenterX=54.9109 CenterY=41.455 CenterZ=0 NormalX=0 NormalY=0 NormalZ=1 AngleXU=0 Radius=1.1
    g51: Circle CenterX=38.9109 CenterY=5.455 CenterZ=0 NormalX=0 NormalY=0 NormalZ=1 AngleXU=0 Radius=1.1
    g52: Circle CenterX=54.9109 CenterY=5.455 CenterZ=0 NormalX=0 NormalY=0 NormalZ=1 AngleXU=0 Radius=1.1
    g53: Circle CenterX=46.9109 CenterY=23.455 CenterZ=0 NormalX=0 NormalY=0 NormalZ=1 AngleXU=0 Radius=1.10183
    g54: GeomPoint X=30.955 Y=23.455 Z=0
  constraints (131):
    c: Coincident(g0,g1)
    c: Coincident(g1,g2)
    c: Coincident(g2,g3)
    c: Coincident(g3,g0)
    c: Horizontal(g0)
    c: Horizontal(g2)
    c: Vertical(g1)
    c: Vertical(g3)
    c: DistanceX(g-1,g0) = 3.4
    c: DistanceY(g-1,g0) = 3.4
    c: DistanceY(g3,g3) = 40.11
    c: DistanceX(g0,g0) = 55.11
    c: PointOnObject(g4,g1)
    c: Horizontal(g4)
    c: Symmetric(g0,g2,g4)
    c: Coincident(g5,g6)
    c: Coincident(g6,g7)
    c: Coincident(g7,g8)
    c: Coincident(g8,g5)
    c: Horizontal(g5)
    c: Horizontal(g7)
    c: Vertical(g6)
    c: Vertical(g8)
    c: PointOnObject(g9,g4)
    c: Symmetric(g6,g5,g9)
    c: Distance(g7) = 20
    c: Distance(g8) = 40
    c: Distance(g5,g0) = 1.6
    c: Coincident(g10,g11)
    c: Coincident(g11,g12)
    c: Coincident(g12,g13)
    c: Coincident(g13,g10)
    c: Horizontal(g10)
    c: Horizontal(g12)
    c: Vertical(g11)
    c: Vertical(g13)
    c: Symmetric(g10,g11,g14)
    c: Symmetric(g7,g5,g15)
    c: Symmetric(g12,g10,g16)
    c: Coincident(g16,g15)
    c: Distance(g13) = 36
    c: Distance(g12) = 16
    c: Tangent(g17,g19) = -1.5708
    c: Tangent(g19,g18) = -1.5708
    c: Tangent(g18,g20) = -1.5708
    c: Tangent(g20,g17) = -1.5708
    c: Equal(g17,g18)
    c: Vertical(g19)
    c: Symmetric(g17,g18,g15)
    c: Tangent(g17,g12)
    c: PointOnObject(g17,g13)
    c: Coincident(g21,g12)
    c: Coincident(g22,g11)
    c: Coincident(g23,g10)
    c: Coincident(g24,g10)
    c: Equal(g21,g22)
    c: Equal(g21,g23)
    c: Equal(g21,g24)
    c: Diameter(g21) = 2.2
    c: PointOnObject(g25,g2)
    c: Vertical(g25)
    c: Symmetric(g0,g0,g25)
    c: Equal(g29,g26)
    c: Equal(g26,g27)
    c: Equal(g27,g28)
    c: Symmetric(g29,g27,g15)
    c: Symmetric(g26,g28,g15)
    c: Horizontal(g26,g29)
    c: Vertical(g29,g28)
    c: Symmetric(g31,g30,g15)
    c: Vertical(g31,g30)
    c: Equal(g31,g30)
    c: Tangent(g30,g17)
    c: PointOnObject(g32,g28)
    c: PointOnObject(g32,g31)
    c: Perpendicular(g28,g32)
    c: Perpendicular(g31,g32)
    c: PointOnObject(g33,g28)
    c: PointOnObject(g33,g29)
    c: Vertical(g33)
    c: Perpendicular(g28,g33)
    c: Equal(g33,g32)
    c: PointOnObject(g34,g28)
    c: PointOnObject(g34,g27)
    c: Horizontal(g34)
    c: Equal(g34,g32)
    c: Tangent(g29,g13)
    c: Perpendicular(g28,g34)
    c: Distance(g34) = 1.4
    c: Coincident(g35,g15)
    c: PointOnObject(g36,g35)
    c: PointOnObject(g36,g29)
    c: Perpendicular(g35,g36)
    c: Perpendicular(g29,g36)
    c: Equal(g36,g34)
    c: PointOnObject(g39,g25)
    c: PointOnObject(g40,g25)
    c: PointOnObject(g41,g25)
    c: PointOnObject(g42,g25)
    c: PointOnObject(g43,g25)
    c: PointOnObject(g44,g25)
    c: Symmetric(g30,g37,g39)
    c: Horizontal(g37,g30)
    c: Symmetric(g31,g38,g42)
    c: Horizontal(g38,g31)
    c: Equal(g38,g37)
    c: Equal(g37,g31)
    c: Equal(g48,g47)
    c: Equal(g47,g45)
    c: Equal(g45,g46)
    c: Equal(g46,g29)
    c: Symmetric(g45,g26,g40)
    c: Horizontal(g45,g26)
    c: Symmetric(g46,g29,g40)
    c: Symmetric(g47,g27,g41)
    c: Horizontal(g47,g27)
    c: Symmetric(g48,g28,g41)
    c: Equal(g52,g51)
    c: Equal(g51,g49)
    c: Equal(g49,g50)
    c: Equal(g50,g21)
    c: Symmetric(g49,g11,g44)
    c: Horizontal(g49,g11)
    c: Symmetric(g12,g50,g44)
    c: Symmetric(g51,g10,g43)
    c: Horizontal(g51,g10)
    c: Symmetric(g52,g10,g43)
    c: PointOnObject(g53,g4)
    c: Equal(g53,g35)
    c: PointOnObject(g54,g25)
    c: Symmetric(g53,g15,g54)
FEATURE [PartDesign::Pocket] Pocket003
  BaseFeature = -> Boolean006
  Direction = (0,0,-1)
  Length = 5
  Length2 = 5
  Profile = -> Sketch020
  ReferenceAxis = -> Sketch020 [N_Axis]
  Type = 1
FEATURE [PartDesign::Hole] Hole002
  BaseFeature = -> Pocket003
  CustomThreadClearance = 0
  Depth = 24
  DepthType = 0
  Diameter = 2.2
  DrillForDepth = false
  DrillPoint = 1
  DrillPointAngle = 118
  HoleCutCountersinkAngle = 90
  HoleCutCustomValues = false
  HoleCutDepth = 1
  HoleCutDiameter = 3.74
  HoleCutType = 1
  ModelThread = false
  Profile = -> Pocket003 [Edge125,Edge95,Edge99,Edge127,Edge133,Edge107,Edge109,Edge137]
  Tapered = false
  TaperedAngle = 90
  ThreadClass = 0
  ThreadDepth = 24
  ThreadDepthType = 0
  ThreadDirection = 0
  ThreadFit = 0
  ThreadSize = 0
  ThreadType = 0
  Threaded = false
  UseCustomThreadClearance = false
  expr: Diameter = 2.2 mm
  expr: HoleCutDiameter = 2.2 mm * 1.7
FEATURE [Sketcher::SketchObject] Sketch025
  FullyConstrained = true
  MapMode = 5
  Placement = pos=(5,-1e-15,1e-15) rot=(0.57735,0.57735,0.57735;2.0944rad)
  expr: Constraints[12] = <<hook>>.apd
  expr: Constraints[13] = <<hook>>.toothd
  expr: Constraints[17] = <<hook>>.toothl
  expr: Constraints[18] = <<hook>>.shaftl
  expr: Constraints[19] = <<hook>>.hmind
  expr: Constraints[22] = <<hook>>.smaxd
  expr: Constraints[23] = <<hook>>.apd
  expr: Constraints[27] = <<hook>>.hmind
  expr: Constraints[28] = <<dim>>.enctsh
  expr: Constraints[42] = <<dim>>.enctsh
  sketch-geometry (15):
    g0: LineSegment StartX=-1.6 StartY=6.5 StartZ=0 EndX=-6.6 EndY=3.9 EndZ=0
    g1: LineSegment StartX=-1.6 StartY=0 StartZ=0 EndX=-4.2 EndY=0 EndZ=0
    g2: LineSegment StartX=-6.6 StartY=3.9 StartZ=0 EndX=-5.45468 EndY=-16 EndZ=0
    g3: LineSegment StartX=-4.2 StartY=0 StartZ=0 EndX=-4.2 EndY=-10 EndZ=0
    g4: LineSegment StartX=-5.45468 StartY=-16 StartZ=0 EndX=-3.85468 EndY=-16 EndZ=0
    g5: LineSegment StartX=-3.85468 StartY=-16 StartZ=0 EndX=-2.1 EndY=-10 EndZ=0
    g6: LineSegment StartX=-4.2 StartY=-10 StartZ=0 EndX=-2.1 EndY=-10 EndZ=0
    g7: LineSegment StartX=-4.2 StartY=-10 StartZ=0 EndX=-4.2 EndY=-16 EndZ=0
    g8: LineSegment StartX=-6.6 StartY=3.9 StartZ=0 EndX=-1.6 EndY=3.9 EndZ=0
    g9: LineSegment StartX=-4.2 StartY=-10 StartZ=0 EndX=-5.8 EndY=-10 EndZ=0
    g10: LineSegment StartX=-1.6 StartY=0 StartZ=0 EndX=-1.6 EndY=3.9 EndZ=0
    g11: LineSegment StartX=-1.6 StartY=6.5 StartZ=0 EndX=0 EndY=7.332 EndZ=0
    g12: LineSegment StartX=-1.6 StartY=3.9 StartZ=0 EndX=-1.6 EndY=6.5 EndZ=0
    g13: LineSegment StartX=-1.6 StartY=3.9 StartZ=0 EndX=0 EndY=3.9 EndZ=0
    g14: LineSegment StartX=0 StartY=3.9 StartZ=0 EndX=0 EndY=7.332 EndZ=0
  constraints (43):
    c: PointOnObject(g10,g-1)
    c: Coincident(g1,g10)
    c: Horizontal(g1)
    c: Coincident(g2,g0)
    c: Coincident(g3,g1)
    c: Vertical(g3)
    c: Coincident(g4,g2)
    c: Horizontal(g4)
    c: Coincident(g5,g4)
    c: Coincident(g6,g3)
    c: Coincident(g6,g5)
    c: Horizontal(g6)
    c: Distance(g1) = 2.6
    c: Distance(g6) = 2.1
    c: Coincident(g7,g3)
    c: PointOnObject(g7,g4)
    c: Vertical(g7)
    c: Distance(g7) = 6
    c: Distance(g3) = 10
    c: Distance(g4) = 1.6
    c: Coincident(g8,g0)
    c: Horizontal(g8)
    c: Distance(g8) = 5
    c: Distance(g8,g0) = 2.6
    c: Coincident(g9,g3)
    c: PointOnObject(g9,g2)
    c: Horizontal(g9)
    c: Distance(g9) = 1.6
    c: Distance(g-1,g10) = 1.6
    c: Vertical(g10)
    c: Distance(g10,g0) = 6.5
    c: Coincident(g10,g8)
    c: Coincident(g11,g0)
    c: Coincident(g12,g8)
    c: Coincident(g12,g0)
    c: Vertical(g12)
    c: Parallel(g11,g0)
    c: Coincident(g13,g8)
    c: Horizontal(g13)
    c: Coincident(g14,g13)
    c: Coincident(g14,g11)
    c: Vertical(g14)
    c: Distance(g13) = 1.6
FEATURE [Sketcher::SketchObject] Sketch027
  FullyConstrained = true
  MapMode = 5
  Placement = pos=(0,0,0) rot=(1,0,0;1.5708rad)
  Support = -> [XZ_Plane054]
  expr: Constraints[17] = (<<hook>>.shouldw - <<hook>>.hookw) / 2
  expr: Constraints[18] = (<<hook>>.shouldw - <<hook>>.hookw) / 2
  expr: Constraints[19] = <<hook>>.hookc
  expr: Constraints[2] = <<dim>>.encrin
  expr: Constraints[5] = <<hook>>.shaftl + <<hook>>.hookl + <<hook>>.hookc
  expr: Constraints[8] = <<hook>>.shouldw
  sketch-geometry (7):
    g0: LineSegment StartX=0 StartY=0 StartZ=0 EndX=5 EndY=0 EndZ=0
    g1: LineSegment StartX=5 StartY=0 StartZ=0 EndX=5 EndY=-16.1 EndZ=0
    g2: LineSegment StartX=5 StartY=-16.1 StartZ=0 EndX=11 EndY=-16.1 EndZ=0
    g3: LineSegment StartX=11 StartY=-16.1 StartZ=0 EndX=11 EndY=0 EndZ=0
    g4: LineSegment StartX=5 StartY=0 StartZ=0 EndX=5.5 EndY=-16 EndZ=0
    g5: LineSegment StartX=5.5 StartY=-16 StartZ=0 EndX=10.5 EndY=-16 EndZ=0
    g6: LineSegment StartX=10.5 StartY=-16 StartZ=0 EndX=11 EndY=0 EndZ=0
  constraints (20):
    c: Coincident(g0,g-1)
    c: PointOnObject(g0,g-1)
    c: Distance(g0) = 5
    c: Coincident(g1,g0)
    c: Vertical(g1)
    c: Distance(g1) = 16.1
    c: Coincident(g2,g1)
    c: Horizontal(g2)
    c: Distance(g2) = 6
    c: Coincident(g3,g2)
    c: PointOnObject(g3,g-1)
    c: Vertical(g3)
    c: Coincident(g4,g0)
    c: Coincident(g5,g4)
    c: Horizontal(g5)
    c: Coincident(g6,g5)
    c: Coincident(g6,g3)
    c: DistanceX(g1,g4) = 0.5
    c: DistanceX(g5,g2) = 0.5
    c: DistanceY(g2,g5) = 0.1
FEATURE [PartDesign::Pad] Pad025
  BaseFeature = -> Hole002
  Direction = (1,0,0)
  Length = 6
  Length2 = 10
  Profile = -> Sketch025
  ReferenceAxis = -> Sketch025 [N_Axis]
  Type = 0
  expr: Length = <<hook>>.shouldw
FEATURE [PartDesign::Pocket] Pocket005
  BaseFeature = -> Pad025
  Direction = (0,1,2e-16)
  Length = 5
  Length2 = 5
  Profile = -> Sketch027
  ReferenceAxis = -> Sketch027 [N_Axis]
  Reversed = true
  Type = 1
FEATURE [PartDesign::Plane] DatumPlane
  AttachmentOffset = pos=(0,0,-23.455) rot=(0,0,1;0rad)
  Length = 60
  MapMode = 2
  Placement = pos=(0,23.455,5.2e-15) rot=(1,0,0;1.5708rad)
  ResizeMode = 0
  Support = -> [XZ_Plane054]
  Width = 60
  expr: .AttachmentOffset.Base.z = -<<dim>>.encw / 2
FEATURE [PartDesign::Plane] DatumPlane005
  AttachmentOffset = pos=(0,0,30.955) rot=(0,0,1;0rad)
  Length = 60
  MapMode = 5
  Placement = pos=(30.955,-6.9e-15,6.9e-15) rot=(0.57735,0.57735,0.57735;2.0944rad)
  ResizeMode = 0
  Support = -> [YZ_Plane054]
  Width = 60
  expr: .AttachmentOffset.Base.z = <<dim>>.encl / 2
FEATURE [PartDesign::Mirrored] Mirrored002
  MirrorPlane = -> DatumPlane005
FEATURE [PartDesign::Mirrored] Mirrored003
  MirrorPlane = -> DatumPlane
FEATURE [PartDesign::MultiTransform] MultiTransform001
  BaseFeature = -> Pocket005
  Originals = -> [Pad025,Pocket005]
  Transformations = -> [Mirrored002,Mirrored003]
FEATURE [PartDesign::Body] Body009
  Group = -> [Sketch017,Pad018,Fillet003,Fillet004,Thickness003,Pad020,Boolean005,Boolean006,DatumPlane001,Sketch020,Pocket003,Hole002,Sketch025,Sketch027,Pad025,Pocket005,DatumPlane,DatumPlane005,MultiTransform001,Mirrored002,Mirrored003]
  Origin = -> Origin055
  Tip = -> MultiTransform001
COMPONENT P11 — recipe-attached ("battery_door", modeled in this document).
Construction recipe (the document's own serialized feature program — sketch geometry with constraints, then the solid features built on it; lengths are millimeters unless a unit is written):

FEATURE [Sketcher::SketchObject] Sketch015
  FullyConstrained = true
  MapMode = 5
  Support = -> [XY_Plane047]
  expr: Constraints[15] = <<dim>>.batl * (1 + <<dim>>.batc) + <<dim>>.enctsh
  expr: Constraints[16] = <<dim>>.batw * (1 + <<dim>>.batc * 2)
  expr: Constraints[26] = <<dim>>.encl / 2
  expr: Constraints[27] = <<dim>>.encw / 2
  expr: Constraints[47] = (<<dim>>.hid + <<dim>>.hit) / 2
  expr: Constraints[48] = <<dim>>.hid / 2 + <<dim>>.enctol / 2
  expr: Constraints[60] = <<dim>>.hid * 3 / 4
  sketch-geometry (24):
    g0: LineSegment StartX=1.28 StartY=6.955 StartZ=0 EndX=60.63 EndY=6.955 EndZ=0
    g1: LineSegment StartX=60.63 StartY=6.955 StartZ=0 EndX=60.63 EndY=39.955 EndZ=0
    g2: LineSegment StartX=60.63 StartY=39.955 StartZ=0 EndX=1.28 EndY=39.955 EndZ=0
    g3: LineSegment StartX=1.28 StartY=39.955 StartZ=0 EndX=1.28 EndY=6.955 EndZ=0
    g4: LineSegment StartX=30.955 StartY=23.455 StartZ=0 EndX=1.28 EndY=23.455 EndZ=0
    g5: LineSegment StartX=1.28 StartY=23.455 StartZ=0 EndX=1.28 EndY=6.955 EndZ=0
    g6: LineSegment StartX=1.28 StartY=6.955 StartZ=0 EndX=30.955 EndY=6.955 EndZ=0
    g7: LineSegment StartX=30.955 StartY=6.955 StartZ=0 EndX=30.955 EndY=23.455 EndZ=0
    g8: LineSegment StartX=0 StartY=0 StartZ=0 EndX=30.955 EndY=0 EndZ=0
    g9: LineSegment StartX=30.955 StartY=0 StartZ=0 EndX=30.955 EndY=23.455 EndZ=0
    g10: LineSegment StartX=30.955 StartY=23.455 StartZ=0 EndX=0 EndY=23.455 EndZ=0
    g11: LineSegment StartX=0 StartY=23.455 StartZ=0 EndX=0 EndY=0 EndZ=0
    g12: ArcOfCircle CenterX=-0.986 CenterY=23.455 CenterZ=0 NormalX=0 NormalY=0 NormalZ=1 AngleXU=0 Radius=3.139 StartAngle=1.5708 EndAngle=4.71239
    g13: ArcOfCircle CenterX=62.896 CenterY=23.455 CenterZ=0 NormalX=0 NormalY=0 NormalZ=1 AngleXU=0 Radius=3.139 StartAngle=4.71239 EndAngle=7.85398
    g14: LineSegment StartX=60.63 StartY=20.316 StartZ=0 EndX=62.896 EndY=20.316 EndZ=0
    g15: LineSegment StartX=-0.986006 StartY=20.316 StartZ=0 EndX=1.28 EndY=20.316 EndZ=0
    g16: LineSegment StartX=1.28 StartY=26.594 StartZ=0 EndX=-0.986 EndY=26.594 EndZ=0
    g17: LineSegment StartX=62.896 StartY=26.594 StartZ=0 EndX=60.63 EndY=26.594 EndZ=0
    g18: LineSegment StartX=1.28 StartY=26.594 StartZ=0 EndX=1.28 EndY=39.955 EndZ=0
    g19: LineSegment StartX=1.28 StartY=20.316 StartZ=0 EndX=1.28 EndY=6.955 EndZ=0
    g20: LineSegment StartX=60.63 StartY=26.594 StartZ=0 EndX=60.63 EndY=39.955 EndZ=0
    g21: LineSegment StartX=60.63 StartY=20.316 StartZ=0 EndX=60.63 EndY=6.955 EndZ=0
    g22: Circle CenterX=-0.986 CenterY=23.455 CenterZ=0 NormalX=0 NormalY=0 NormalZ=1 AngleXU=0 Radius=1.60425
    g23: Circle CenterX=62.896 CenterY=23.455 CenterZ=0 NormalX=0 NormalY=0 NormalZ=1 AngleXU=0 Radius=1.60425
  constraints (61):
    c: Coincident(g0,g1)
    c: Coincident(g1,g2)
    c: Coincident(g2,g3)
    c: Coincident(g3,g0)
    c: Horizontal(g0)
    c: Horizontal(g2)
    c: Vertical(g1)
    c: Vertical(g3)
    c: Coincident(g4,g5)
    c: Coincident(g5,g6)
    c: Coincident(g6,g7)
    c: Coincident(g7,g4)
    c: Horizontal(g4)
    c: Vertical(g7)
    c: Coincident(g5,g0)
    c: Distance(g2) = 59.35
    c: Distance(g1) = 33
    c: Coincident(g8,g9)
    c: Coincident(g9,g10)
    c: Coincident(g10,g11)
    c: Coincident(g11,g8)
    c: Horizontal(g8)
    c: Horizontal(g10)
    c: Vertical(g9)
    c: Vertical(g11)
    c: Coincident(g8,g-1)
    c: Distance(g10) = 30.955
    c: Distance(g9) = 23.455
    c: Coincident(g4,g9)
    c: Symmetric(g0,g0,g6)
    c: Symmetric(g0,g2,g4)
    c: Coincident(g12,g15) = -1.5708
    c: Coincident(g14,g13) = -1.5708
    c: Equal(g12,g13)
    c: PointOnObject(g12,g10)
    c: Horizontal(g14)
    c: Horizontal(g15)
    c: PointOnObject(g16,g3)
    c: PointOnObject(g14,g1)
    c: PointOnObject(g17,g1)
    c: Symmetric(g12,g13,g4)
    c: Horizontal(g16)
    c: Horizontal(g17)
    c: Tangent(g16,g12) = -1.5708
    c: Tangent(g13,g17) = -1.5708
    c: Symmetric(g15,g16,g4)
    c: Horizontal(g15,g14)
    c: Radius(g12) = 3.139
    c: Distance(g16) = 2.266
    c: Coincident(g18,g16)
    c: Coincident(g18,g2)
    c: Coincident(g19,g15)
    c: Coincident(g19,g0)
    c: Coincident(g20,g17)
    c: Coincident(g20,g1)
    c: Coincident(g21,g14)
    c: Coincident(g21,g0)
    c: Coincident(g22,g12)
    c: Coincident(g23,g13)
    c: Equal(g23,g22)
    c: Diameter(g22) = 3.2085
FEATURE [PartDesign::Pad] Pad016
  Direction = (0,0,1)
  Length = 1.6
  Length2 = 10
  Profile = -> Sketch015
  ReferenceAxis = -> Sketch015 [N_Axis]
  Reversed = true
  Type = 0
  expr: Length = <<dim>>.enctsh
FEATURE [PartDesign::Body] Body007  label="batterydoor"
  Group = -> [Sketch015,Pad016]
  Origin = -> Origin052
  Tip = -> Pad016
  expr: .Placement.Base.z = 0
COMPONENT P12 — recipe-attached ("standoff1", modeled in this document).
Construction recipe (the document's own serialized feature program — sketch geometry with constraints, then the solid features built on it; lengths are millimeters unless a unit is written):

FEATURE [PartDesign::CoordinateSystem] LCS_0
  AttacherType = Attacher::AttachEngine3D
  MapMode = 2
  Support = -> [X_Axis040]
FEATURE [Sketcher::SketchObject] Sketch002
  FullyConstrained = true
  MapMode = 5
  Support = -> [XY_Plane040]
  expr: Constraints[11] = <<dim>>.pcbh2x
  expr: Constraints[12] = <<dim>>.pcbh2y
  expr: Constraints[13] = <<dim>>.pcbh3x
  expr: Constraints[14] = <<dim>>.pcbh3y
  expr: Constraints[15] = <<dim>>.pcbh4x
  expr: Constraints[16] = <<dim>>.pcbh4y
  expr: Constraints[17] = <<dim>>.pcbh1x
  expr: Constraints[18] = <<dim>>.pcbh1y
  expr: Constraints[2] = <<dim>>.hid
  expr: Constraints[30] = <<dim>>.hit
  expr: Constraints[41] = <<dim>>.encl / 2
  expr: Constraints[42] = <<dim>>.encw / 2
  expr: Constraints[44] = <<dim>>.pcbl / 2
  expr: Constraints[45] = <<dim>>.pcbw / 2
  sketch-geometry (17):
    g0: Circle CenterX=7.289 CenterY=39.62 CenterZ=0 NormalX=0 NormalY=0 NormalZ=1 AngleXU=0 Radius=2.139
    g1: Circle CenterX=16.687 CenterY=7.362 CenterZ=0 NormalX=0 NormalY=0 NormalZ=1 AngleXU=0 Radius=2.139
    g2: Circle CenterX=53.618 CenterY=39.584 CenterZ=0 NormalX=0 NormalY=0 NormalZ=1 AngleXU=0 Radius=2.139
    g3: Circle CenterX=53.618 CenterY=7.326 CenterZ=0 NormalX=0 NormalY=0 NormalZ=1 AngleXU=0 Radius=2.139
    g4: LineSegment StartX=30.955 StartY=23.455 StartZ=0 EndX=2.5 EndY=23.455 EndZ=0
    g5: LineSegment StartX=2.5 StartY=23.455 StartZ=0 EndX=2.5 EndY=2.5 EndZ=0
    g6: LineSegment StartX=2.5 StartY=2.5 StartZ=0 EndX=30.955 EndY=2.5 EndZ=0
    g7: LineSegment StartX=30.955 StartY=2.5 StartZ=0 EndX=30.955 EndY=23.455 EndZ=0
    g8: Circle CenterX=7.289 CenterY=39.62 CenterZ=0 NormalX=0 NormalY=0 NormalZ=1 AngleXU=0 Radius=4.139
    g9: Circle CenterX=16.687 CenterY=7.362 CenterZ=0 NormalX=0 NormalY=0 NormalZ=1 AngleXU=0 Radius=4.139
    g10: Circle CenterX=53.618 CenterY=7.326 CenterZ=0 NormalX=0 NormalY=0 NormalZ=1 AngleXU=0 Radius=4.139
    g11: Circle CenterX=53.618 CenterY=39.584 CenterZ=0 NormalX=0 NormalY=0 NormalZ=1 AngleXU=0 Radius=4.139
    g12: LineSegment StartX=14.548 StartY=7.362 StartZ=0 EndX=12.548 EndY=7.362 EndZ=0
    g13: LineSegment StartX=0 StartY=0 StartZ=0 EndX=30.955 EndY=0 EndZ=0
    g14: LineSegment StartX=30.955 StartY=0 StartZ=0 EndX=30.955 EndY=23.455 EndZ=0
    g15: LineSegment StartX=30.955 StartY=23.455 StartZ=0 EndX=0 EndY=23.455 EndZ=0
    g16: LineSegment StartX=0 StartY=23.455 StartZ=0 EndX=0 EndY=0 EndZ=0
  constraints (46):
    c: Equal(g1,g3)
    c: Equal(g3,g2)
    c: Diameter(g1) = 4.278
    c: Coincident(g4,g5)
    c: Coincident(g5,g6)
    c: Coincident(g6,g7)
    c: Coincident(g7,g4)
    c: Horizontal(g4)
    c: Horizontal(g6)
    c: Vertical(g5)
    c: Vertical(g7)
    c: DistanceX(g5,g2) = 51.118
    c: DistanceY(g5,g2) = 37.084
    c: DistanceX(g5,g3) = 51.118
    c: DistanceY(g5,g3) = 4.826
    c: DistanceX(g5,g1) = 14.187
    c: DistanceY(g5,g1) = 4.862
    c: DistanceX(g5,g0) = 4.789
    c: DistanceY(g5,g0) = 37.12
    c: Coincident(g8,g0)
    c: Coincident(g9,g1)
    c: Coincident(g10,g3)
    c: Coincident(g11,g2)
    c: Equal(g8,g11)
    c: Equal(g11,g10)
    c: Equal(g10,g9)
    c: PointOnObject(g12,g1)
    c: PointOnObject(g12,g9)
    c: Horizontal(g12)
    c: Horizontal(g12,g1)
    c: Distance(g12) = 2
    c: Equal(g0,g1)
    c: Coincident(g13,g14)
    c: Coincident(g14,g15)
    c: Coincident(g15,g16)
    c: Coincident(g16,g13)
    c: Horizontal(g13)
    c: Horizontal(g15)
    c: Vertical(g14)
    c: Vertical(g16)
    c: Coincident(g13,g-1)
    c: Distance(g15) = 30.955
    c: Distance(g14) = 23.455
    c: Coincident(g4,g14)
    c: Distance(g6) = 28.455
    c: Distance(g5) = 20.955
FEATURE [PartDesign::Pad] Pad003
  Direction = (0,0,1)
  Length = 26.935
  Length2 = 10
  Profile = -> Sketch002
  ReferenceAxis = -> Sketch002 [N_Axis]
  Type = 0
  expr: Length = <<dim>>.ench - <<dim>>.pcbh
FEATURE [PartDesign::Body] standoffs  label="standoff1"
  Group = -> [LCS_0,Sketch002,Pad003]
  Origin = -> Origin040
  Tip = -> Pad003
COMPONENT P13 — recipe-attached ("standoff2", modeled in this document).
Construction recipe (the document's own serialized feature program — sketch geometry with constraints, then the solid features built on it; lengths are millimeters unless a unit is written):

FEATURE [Sketcher::SketchObject] Sketch007
  FullyConstrained = true
  MapMode = 5
  Support = -> [XY_Plane040]
  expr: Constraints[11] = <<dim>>.pcbh2x
  expr: Constraints[12] = <<dim>>.pcbh2y
  expr: Constraints[13] = <<dim>>.pcbh3x
  expr: Constraints[14] = <<dim>>.pcbh3y
  expr: Constraints[15] = <<dim>>.pcbh4x
  expr: Constraints[16] = <<dim>>.pcbh4y
  expr: Constraints[17] = <<dim>>.pcbh1x
  expr: Constraints[18] = <<dim>>.pcbh1y
  expr: Constraints[2] = <<dim>>.hid
  expr: Constraints[30] = <<dim>>.hit
  expr: Constraints[41] = <<dim>>.encl / 2
  expr: Constraints[42] = <<dim>>.encw / 2
  expr: Constraints[44] = <<dim>>.pcbl / 2
  expr: Constraints[45] = <<dim>>.pcbw / 2
  sketch-geometry (17):
    g0: Circle CenterX=7.289 CenterY=39.62 CenterZ=0 NormalX=0 NormalY=0 NormalZ=1 AngleXU=0 Radius=2.139
    g1: Circle CenterX=16.687 CenterY=7.362 CenterZ=0 NormalX=0 NormalY=0 NormalZ=1 AngleXU=0 Radius=2.139
    g2: Circle CenterX=53.618 CenterY=39.584 CenterZ=0 NormalX=0 NormalY=0 NormalZ=1 AngleXU=0 Radius=2.139
    g3: Circle CenterX=53.618 CenterY=7.326 CenterZ=0 NormalX=0 NormalY=0 NormalZ=1 AngleXU=0 Radius=2.139
    g4: LineSegment StartX=30.955 StartY=23.455 StartZ=0 EndX=2.5 EndY=23.455 EndZ=0
    g5: LineSegment StartX=2.5 StartY=23.455 StartZ=0 EndX=2.5 EndY=2.5 EndZ=0
    g6: LineSegment StartX=2.5 StartY=2.5 StartZ=0 EndX=30.955 EndY=2.5 EndZ=0
    g7: LineSegment StartX=30.955 StartY=2.5 StartZ=0 EndX=30.955 EndY=23.455 EndZ=0
    g8: Circle CenterX=7.289 CenterY=39.62 CenterZ=0 NormalX=0 NormalY=0 NormalZ=1 AngleXU=0 Radius=4.139
    g9: Circle CenterX=16.687 CenterY=7.362 CenterZ=0 NormalX=0 NormalY=0 NormalZ=1 AngleXU=0 Radius=4.139
    g10: Circle CenterX=53.618 CenterY=7.326 CenterZ=0 NormalX=0 NormalY=0 NormalZ=1 AngleXU=0 Radius=4.139
    g11: Circle CenterX=53.618 CenterY=39.584 CenterZ=0 NormalX=0 NormalY=0 NormalZ=1 AngleXU=0 Radius=4.139
    g12: LineSegment StartX=14.548 StartY=7.362 StartZ=0 EndX=12.548 EndY=7.362 EndZ=0
    g13: LineSegment StartX=0 StartY=0 StartZ=0 EndX=30.955 EndY=0 EndZ=0
    g14: LineSegment StartX=30.955 StartY=0 StartZ=0 EndX=30.955 EndY=23.455 EndZ=0
    g15: LineSegment StartX=30.955 StartY=23.455 StartZ=0 EndX=0 EndY=23.455 EndZ=0
    g16: LineSegment StartX=0 StartY=23.455 StartZ=0 EndX=0 EndY=0 EndZ=0
  constraints (46):
    c: Equal(g1,g3)
    c: Equal(g3,g2)
    c: Diameter(g1) = 4.278
    c: Coincident(g4,g5)
    c: Coincident(g5,g6)
    c: Coincident(g6,g7)
    c: Coincident(g7,g4)
    c: Horizontal(g4)
    c: Horizontal(g6)
    c: Vertical(g5)
    c: Vertical(g7)
    c: DistanceX(g5,g2) = 51.118
    c: DistanceY(g5,g2) = 37.084
    c: DistanceX(g5,g3) = 51.118
    c: DistanceY(g5,g3) = 4.826
    c: DistanceX(g5,g1) = 14.187
    c: DistanceY(g5,g1) = 4.862
    c: DistanceX(g5,g0) = 4.789
    c: DistanceY(g5,g0) = 37.12
    c: Coincident(g8,g0)
    c: Coincident(g9,g1)
    c: Coincident(g10,g3)
    c: Coincident(g11,g2)
    c: Equal(g8,g11)
    c: Equal(g11,g10)
    c: Equal(g10,g9)
    c: PointOnObject(g12,g1)
    c: PointOnObject(g12,g9)
    c: Horizontal(g12)
    c: Horizontal(g12,g1)
    c: Distance(g12) = 2
    c: Equal(g0,g1)
    c: Coincident(g13,g14)
    c: Coincident(g14,g15)
    c: Coincident(g15,g16)
    c: Coincident(g16,g13)
    c: Horizontal(g13)
    c: Horizontal(g15)
    c: Vertical(g14)
    c: Vertical(g16)
    c: Coincident(g13,g-1)
    c: Distance(g15) = 30.955
    c: Distance(g14) = 23.455
    c: Coincident(g4,g14)
    c: Distance(g6) = 28.455
    c: Distance(g5) = 20.955
FEATURE [PartDesign::Pad] Pad007
  Direction = (0,0,1)
  Length = 26.935
  Length2 = 10
  Profile = -> Sketch007
  ReferenceAxis = -> Sketch007 [N_Axis]
  Type = 0
  expr: Length = <<dim>>.ench - <<dim>>.pcbh
FEATURE [PartDesign::Body] standoffs004  label="standoff2"
  Group = -> [Sketch007,Pad007]
  Origin = -> Origin045
  Tip = -> Pad007
COMPONENT P14 — recipe-attached ("standoff3", modeled in this document).
Construction recipe (the document's own serialized feature program — sketch geometry with constraints, then the solid features built on it; lengths are millimeters unless a unit is written):

FEATURE [Sketcher::SketchObject] Sketch008
  FullyConstrained = true
  MapMode = 5
  Support = -> [XY_Plane040]
  expr: Constraints[11] = <<dim>>.pcbh2x
  expr: Constraints[12] = <<dim>>.pcbh2y
  expr: Constraints[13] = <<dim>>.pcbh3x
  expr: Constraints[14] = <<dim>>.pcbh3y
  expr: Constraints[15] = <<dim>>.pcbh4x
  expr: Constraints[16] = <<dim>>.pcbh4y
  expr: Constraints[17] = <<dim>>.pcbh1x
  expr: Constraints[18] = <<dim>>.pcbh1y
  expr: Constraints[2] = <<dim>>.hid
  expr: Constraints[30] = <<dim>>.hit
  expr: Constraints[41] = <<dim>>.encl / 2
  expr: Constraints[42] = <<dim>>.encw / 2
  expr: Constraints[44] = <<dim>>.pcbl / 2
  expr: Constraints[45] = <<dim>>.pcbw / 2
  sketch-geometry (17):
    g0: Circle CenterX=7.289 CenterY=39.62 CenterZ=0 NormalX=0 NormalY=0 NormalZ=1 AngleXU=0 Radius=2.139
    g1: Circle CenterX=16.687 CenterY=7.362 CenterZ=0 NormalX=0 NormalY=0 NormalZ=1 AngleXU=0 Radius=2.139
    g2: Circle CenterX=53.618 CenterY=39.584 CenterZ=0 NormalX=0 NormalY=0 NormalZ=1 AngleXU=0 Radius=2.139
    g3: Circle CenterX=53.618 CenterY=7.326 CenterZ=0 NormalX=0 NormalY=0 NormalZ=1 AngleXU=0 Radius=2.139
    g4: LineSegment StartX=30.955 StartY=23.455 StartZ=0 EndX=2.5 EndY=23.455 EndZ=0
    g5: LineSegment StartX=2.5 StartY=23.455 StartZ=0 EndX=2.5 EndY=2.5 EndZ=0
    g6: LineSegment StartX=2.5 StartY=2.5 StartZ=0 EndX=30.955 EndY=2.5 EndZ=0
    g7: LineSegment StartX=30.955 StartY=2.5 StartZ=0 EndX=30.955 EndY=23.455 EndZ=0
    g8: Circle CenterX=7.289 CenterY=39.62 CenterZ=0 NormalX=0 NormalY=0 NormalZ=1 AngleXU=0 Radius=4.139
    g9: Circle CenterX=16.687 CenterY=7.362 CenterZ=0 NormalX=0 NormalY=0 NormalZ=1 AngleXU=0 Radius=4.139
    g10: Circle CenterX=53.618 CenterY=7.326 CenterZ=0 NormalX=0 NormalY=0 NormalZ=1 AngleXU=0 Radius=4.139
    g11: Circle CenterX=53.618 CenterY=39.584 CenterZ=0 NormalX=0 NormalY=0 NormalZ=1 AngleXU=0 Radius=4.139
    g12: LineSegment StartX=14.548 StartY=7.362 StartZ=0 EndX=12.548 EndY=7.362 EndZ=0
    g13: LineSegment StartX=0 StartY=0 StartZ=0 EndX=30.955 EndY=0 EndZ=0
    g14: LineSegment StartX=30.955 StartY=0 StartZ=0 EndX=30.955 EndY=23.455 EndZ=0
    g15: LineSegment StartX=30.955 StartY=23.455 StartZ=0 EndX=0 EndY=23.455 EndZ=0
    g16: LineSegment StartX=0 StartY=23.455 StartZ=0 EndX=0 EndY=0 EndZ=0
  constraints (46):
    c: Equal(g1,g3)
    c: Equal(g3,g2)
    c: Diameter(g1) = 4.278
    c: Coincident(g4,g5)
    c: Coincident(g5,g6)
    c: Coincident(g6,g7)
    c: Coincident(g7,g4)
    c: Horizontal(g4)
    c: Horizontal(g6)
    c: Vertical(g5)
    c: Vertical(g7)
    c: DistanceX(g5,g2) = 51.118
    c: DistanceY(g5,g2) = 37.084
    c: DistanceX(g5,g3) = 51.118
    c: DistanceY(g5,g3) = 4.826
    c: DistanceX(g5,g1) = 14.187
    c: DistanceY(g5,g1) = 4.862
    c: DistanceX(g5,g0) = 4.789
    c: DistanceY(g5,g0) = 37.12
    c: Coincident(g8,g0)
    c: Coincident(g9,g1)
    c: Coincident(g10,g3)
    c: Coincident(g11,g2)
    c: Equal(g8,g11)
    c: Equal(g11,g10)
    c: Equal(g10,g9)
    c: PointOnObject(g12,g1)
    c: PointOnObject(g12,g9)
    c: Horizontal(g12)
    c: Horizontal(g12,g1)
    c: Distance(g12) = 2
    c: Equal(g0,g1)
    c: Coincident(g13,g14)
    c: Coincident(g14,g15)
    c: Coincident(g15,g16)
    c: Coincident(g16,g13)
    c: Horizontal(g13)
    c: Horizontal(g15)
    c: Vertical(g14)
    c: Vertical(g16)
    c: Coincident(g13,g-1)
    c: Distance(g15) = 30.955
    c: Distance(g14) = 23.455
    c: Coincident(g4,g14)
    c: Distance(g6) = 28.455
    c: Distance(g5) = 20.955
FEATURE [PartDesign::Pad] Pad008
  Direction = (0,0,1)
  Length = 26.935
  Length2 = 10
  Profile = -> Sketch008
  ReferenceAxis = -> Sketch008 [N_Axis]
  Type = 0
  expr: Length = <<dim>>.ench - <<dim>>.pcbh
FEATURE [PartDesign::Body] standoffs005  label="standoff3"
  Group = -> [Sketch008,Pad008]
  Origin = -> Origin046
  Tip = -> Pad008
COMPONENT P15 — recipe-attached ("standoff4", modeled in this document).
Construction recipe (the document's own serialized feature program — sketch geometry with constraints, then the solid features built on it; lengths are millimeters unless a unit is written):

FEATURE [Sketcher::SketchObject] Sketch009
  FullyConstrained = true
  MapMode = 5
  Support = -> [XY_Plane040]
  expr: Constraints[11] = <<dim>>.pcbh2x
  expr: Constraints[12] = <<dim>>.pcbh2y
  expr: Constraints[13] = <<dim>>.pcbh3x
  expr: Constraints[14] = <<dim>>.pcbh3y
  expr: Constraints[15] = <<dim>>.pcbh4x
  expr: Constraints[16] = <<dim>>.pcbh4y
  expr: Constraints[17] = <<dim>>.pcbh1x
  expr: Constraints[18] = <<dim>>.pcbh1y
  expr: Constraints[2] = <<dim>>.hid
  expr: Constraints[30] = <<dim>>.hit
  expr: Constraints[41] = <<dim>>.encl / 2
  expr: Constraints[42] = <<dim>>.encw / 2
  expr: Constraints[44] = <<dim>>.pcbl / 2
  expr: Constraints[45] = <<dim>>.pcbw / 2
  sketch-geometry (17):
    g0: Circle CenterX=7.289 CenterY=39.62 CenterZ=0 NormalX=0 NormalY=0 NormalZ=1 AngleXU=0 Radius=2.139
    g1: Circle CenterX=16.687 CenterY=7.362 CenterZ=0 NormalX=0 NormalY=0 NormalZ=1 AngleXU=0 Radius=2.139
    g2: Circle CenterX=53.618 CenterY=39.584 CenterZ=0 NormalX=0 NormalY=0 NormalZ=1 AngleXU=0 Radius=2.139
    g3: Circle CenterX=53.618 CenterY=7.326 CenterZ=0 NormalX=0 NormalY=0 NormalZ=1 AngleXU=0 Radius=2.139
    g4: LineSegment StartX=30.955 StartY=23.455 StartZ=0 EndX=2.5 EndY=23.455 EndZ=0
    g5: LineSegment StartX=2.5 StartY=23.455 StartZ=0 EndX=2.5 EndY=2.5 EndZ=0
    g6: LineSegment StartX=2.5 StartY=2.5 StartZ=0 EndX=30.955 EndY=2.5 EndZ=0
    g7: LineSegment StartX=30.955 StartY=2.5 StartZ=0 EndX=30.955 EndY=23.455 EndZ=0
    g8: Circle CenterX=7.289 CenterY=39.62 CenterZ=0 NormalX=0 NormalY=0 NormalZ=1 AngleXU=0 Radius=4.139
    g9: Circle CenterX=16.687 CenterY=7.362 CenterZ=0 NormalX=0 NormalY=0 NormalZ=1 AngleXU=0 Radius=4.139
    g10: Circle CenterX=53.618 CenterY=7.326 CenterZ=0 NormalX=0 NormalY=0 NormalZ=1 AngleXU=0 Radius=4.139
    g11: Circle CenterX=53.618 CenterY=39.584 CenterZ=0 NormalX=0 NormalY=0 NormalZ=1 AngleXU=0 Radius=4.139
    g12: LineSegment StartX=14.548 StartY=7.362 StartZ=0 EndX=12.548 EndY=7.362 EndZ=0
    g13: LineSegment StartX=0 StartY=0 StartZ=0 EndX=30.955 EndY=0 EndZ=0
    g14: LineSegment StartX=30.955 StartY=0 StartZ=0 EndX=30.955 EndY=23.455 EndZ=0
    g15: LineSegment StartX=30.955 StartY=23.455 StartZ=0 EndX=0 EndY=23.455 EndZ=0
    g16: LineSegment StartX=0 StartY=23.455 StartZ=0 EndX=0 EndY=0 EndZ=0
  constraints (46):
    c: Equal(g1,g3)
    c: Equal(g3,g2)
    c: Diameter(g1) = 4.278
    c: Coincident(g4,g5)
    c: Coincident(g5,g6)
    c: Coincident(g6,g7)
    c: Coincident(g7,g4)
    c: Horizontal(g4)
    c: Horizontal(g6)
    c: Vertical(g5)
    c: Vertical(g7)
    c: DistanceX(g5,g2) = 51.118
    c: DistanceY(g5,g2) = 37.084
    c: DistanceX(g5,g3) = 51.118
    c: DistanceY(g5,g3) = 4.826
    c: DistanceX(g5,g1) = 14.187
    c: DistanceY(g5,g1) = 4.862
    c: DistanceX(g5,g0) = 4.789
    c: DistanceY(g5,g0) = 37.12
    c: Coincident(g8,g0)
    c: Coincident(g9,g1)
    c: Coincident(g10,g3)
    c: Coincident(g11,g2)
    c: Equal(g8,g11)
    c: Equal(g11,g10)
    c: Equal(g10,g9)
    c: PointOnObject(g12,g1)
    c: PointOnObject(g12,g9)
    c: Horizontal(g12)
    c: Horizontal(g12,g1)
    c: Distance(g12) = 2
    c: Equal(g0,g1)
    c: Coincident(g13,g14)
    c: Coincident(g14,g15)
    c: Coincident(g15,g16)
    c: Coincident(g16,g13)
    c: Horizontal(g13)
    c: Horizontal(g15)
    c: Vertical(g14)
    c: Vertical(g16)
    c: Coincident(g13,g-1)
    c: Distance(g15) = 30.955
    c: Distance(g14) = 23.455
    c: Coincident(g4,g14)
    c: Distance(g6) = 28.455
    c: Distance(g5) = 20.955
FEATURE [PartDesign::Pad] Pad009
  Direction = (0,0,1)
  Length = 26.935
  Length2 = 10
  Profile = -> Sketch009
  ReferenceAxis = -> Sketch009 [N_Axis]
  Type = 0
  expr: Length = <<dim>>.ench - <<dim>>.pcbh
FEATURE [PartDesign::Body] standoffs006  label="standoff4"
  Group = -> [Sketch009,Pad009]
  Origin = -> Origin047
  Tip = -> Pad009
PROVENANCE & LICENSES
A FreeCAD (.FCStd) document from a public repository crawl; recipes are the document's own serialized feature recipes (and, for linked parts, companion documents' recipes).
License: as declared in the source repository (recorded in the dataset sidecar).
